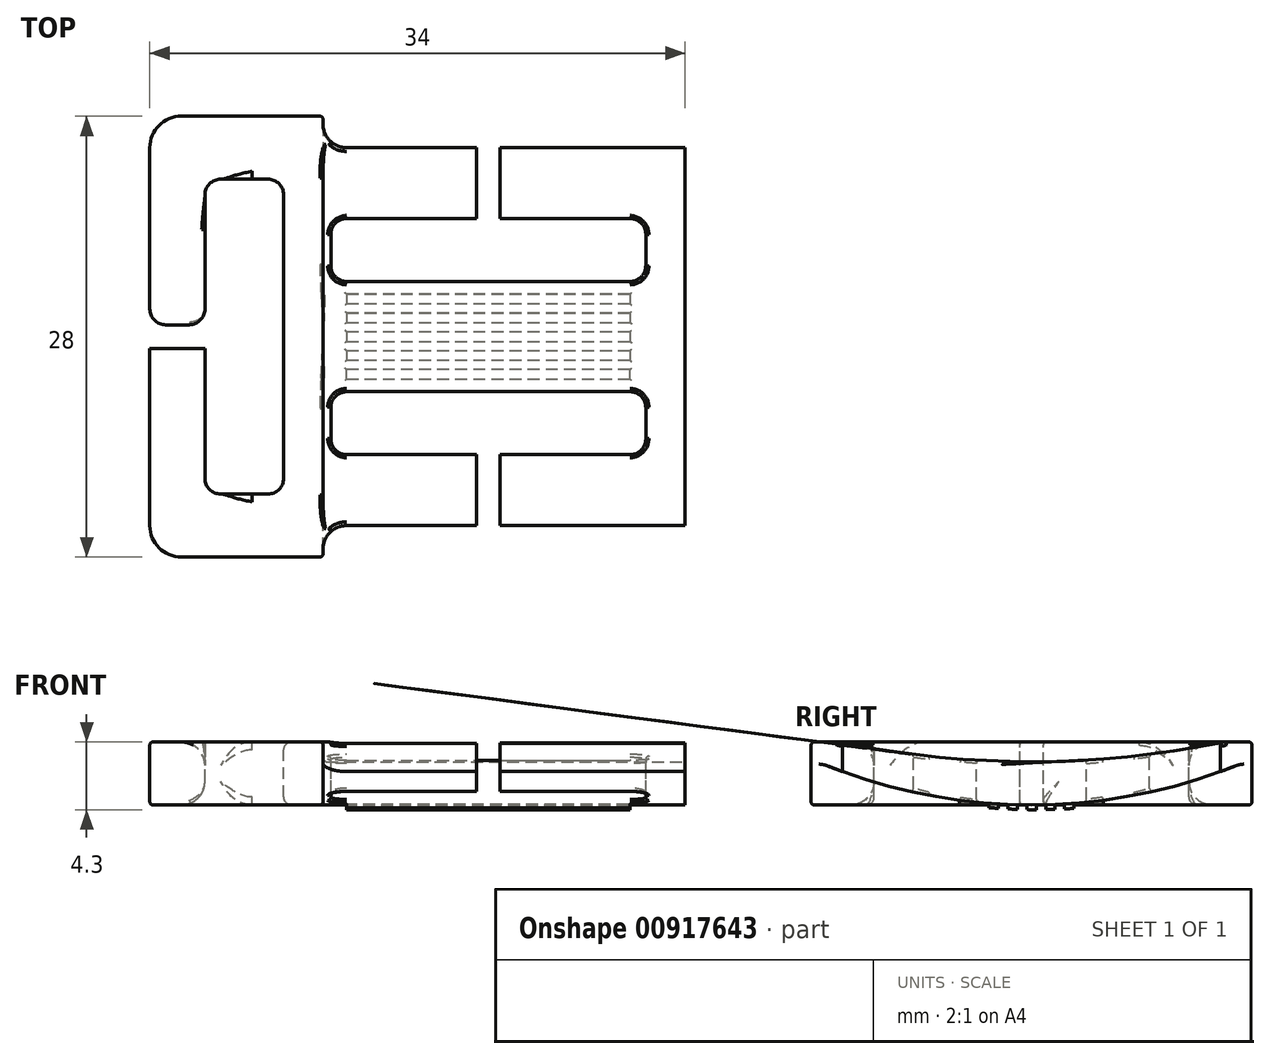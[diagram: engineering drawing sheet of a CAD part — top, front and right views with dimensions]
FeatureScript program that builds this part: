
annotation { "Feature Type Name" : "Feature", "Feature Type Description" : "" }
export const myFeature = defineFeature(function(context is Context, id is Id, definition is map)
    precondition{}
    {
        {
            var Q0;
            Q0=qCreatedBy(makeId("Top.planeOp"),FACE);
            var sketch = newSketch(context, id + "F0", { "sketchPlane" : qUnion([Q0])});
            skLineSegment(sketch, "E0.bottom", {"start": v(0, 0) * mm, "end": v(34, 0) * mm});
            skLineSegment(sketch, "E0.top", {"start": v(0, 28) * mm, "end": v(34, 28) * mm});
            skLineSegment(sketch, "E0.left", {"start": v(0, 0) * mm, "end": v(0, 28) * mm});
            skLineSegment(sketch, "E0.right", {"start": v(34, 0) * mm, "end": v(34, 28) * mm});
            skSolve(sketch);
        }
        {
            var Q0;
            Q0 = qSketchRegion(id + "F0", true);
            extrude(context, id + "F1", {"entities" : qUnion([Q0]), "depth" : 4 * mm, "offsetDistance" : 25 * mm});
        }
        {
            var Q0;
            Q0=makeQuery(id+"F1.opExtrude","CAP_FACE",FACE,{"disambiguationData":[OSD([sQuery(id+"F0.wireOp",EDGE,"E0.bottom"),sQuery(id+"F0.wireOp",EDGE,"E0.top"),sQuery(id+"F0.wireOp",EDGE,"E0.left"),sQuery(id+"F0.wireOp",EDGE,"E0.right")])],"isStart":false});
            var sketch = newSketch(context, id + "F2", { "sketchPlane" : qUnion([Q0])});
            skLineSegment(sketch, "E1.bottom", {"start": v(3.5, 24) * mm, "end": v(8.5, 24) * mm});
            skLineSegment(sketch, "E1.top", {"start": v(3.5, 4) * mm, "end": v(8.5, 4) * mm});
            skLineSegment(sketch, "E1.left", {"start": v(3.5, 24) * mm, "end": v(3.5, 4) * mm});
            skLineSegment(sketch, "E1.right", {"start": v(8.5, 24) * mm, "end": v(8.5, 4) * mm});
            skSolve(sketch);
        }
        {
            var Q0;
            Q0 = qSketchRegion(id + "F2", true);
            extrude(context, id + "F3", {"entities" : qUnion([Q0]), "operationType" : NewBodyOperationType.REMOVE, "endBound" : BoundingType.THROUGH_ALL, "oppositeDirection" : true, "depth" : 25 * mm, "offsetDistance" : 25 * mm});
        }
        {
            var Q0;
            Q0=makeQuery(id+"F1.opExtrude","CAP_FACE",FACE,{"disambiguationData":[OSD([sQuery(id+"F0.wireOp",EDGE,"E0.bottom"),sQuery(id+"F0.wireOp",EDGE,"E0.top"),sQuery(id+"F0.wireOp",EDGE,"E0.left"),sQuery(id+"F0.wireOp",EDGE,"E0.right")])],"isStart":false});
            var sketch = newSketch(context, id + "F4", { "sketchPlane" : qUnion([Q0])});
            skLineSegment(sketch, "E2.bottom", {"start": v(11.5, 21.5) * mm, "end": v(31.5, 21.5) * mm});
            skLineSegment(sketch, "E2.top", {"start": v(11.5, 17.5) * mm, "end": v(31.5, 17.5) * mm});
            skLineSegment(sketch, "E2.left", {"start": v(11.5, 21.5) * mm, "end": v(11.5, 17.5) * mm});
            skLineSegment(sketch, "E2.right", {"start": v(31.5, 21.5) * mm, "end": v(31.5, 17.5) * mm});
            skLineSegment(sketch, "E3.bottom", {"start": v(11.5, 10.5) * mm, "end": v(31.5, 10.5) * mm});
            skLineSegment(sketch, "E3.top", {"start": v(11.5, 6.5) * mm, "end": v(31.5, 6.5) * mm});
            skLineSegment(sketch, "E3.left", {"start": v(11.5, 10.5) * mm, "end": v(11.5, 6.5) * mm});
            skLineSegment(sketch, "E3.right", {"start": v(31.5, 10.5) * mm, "end": v(31.5, 6.5) * mm});
            skSolve(sketch);
        }
        {
            var Q0;
            Q0 = qSketchRegion(id + "F4", true);
            extrude(context, id + "F5", {"entities" : qUnion([Q0]), "operationType" : NewBodyOperationType.REMOVE, "endBound" : BoundingType.THROUGH_ALL, "oppositeDirection" : true, "depth" : 25 * mm, "offsetDistance" : 25 * mm});
        }
        {
            var Q0;
            Q0=makeQuery(id+"F1.opExtrude","CAP_FACE",FACE,{"disambiguationData":[OSD([sQuery(id+"F0.wireOp",EDGE,"E0.bottom"),sQuery(id+"F0.wireOp",EDGE,"E0.top"),sQuery(id+"F0.wireOp",EDGE,"E0.left"),sQuery(id+"F0.wireOp",EDGE,"E0.right")])],"isStart":false});
            var sketch = newSketch(context, id + "F6", { "sketchPlane" : qUnion([Q0])});
            skLineSegment(sketch, "E4.bottom", {"start": v(0, 13.25) * mm, "end": v(3.5, 13.25) * mm});
            skLineSegment(sketch, "E4.top", {"start": v(0, 14.75) * mm, "end": v(3.5, 14.75) * mm});
            skLineSegment(sketch, "E4.left", {"start": v(0, 13.25) * mm, "end": v(0, 14.75) * mm});
            skLineSegment(sketch, "E4.right", {"start": v(3.5, 13.25) * mm, "end": v(3.5, 14.75) * mm});
            skLineSegment(sketch, "E5.bottom", {"start": v(20.75, 28) * mm, "end": v(22.25, 28) * mm});
            skLineSegment(sketch, "E5.top", {"start": v(20.75, 21.5) * mm, "end": v(22.25, 21.5) * mm});
            skLineSegment(sketch, "E5.left", {"start": v(20.75, 28) * mm, "end": v(20.75, 21.5) * mm});
            skLineSegment(sketch, "E5.right", {"start": v(22.25, 28) * mm, "end": v(22.25, 21.5) * mm});
            skLineSegment(sketch, "E6.bottom", {"start": v(20.75, 6.5) * mm, "end": v(22.25, 6.5) * mm});
            skLineSegment(sketch, "E6.top", {"start": v(20.75, 0) * mm, "end": v(22.25, 0) * mm});
            skLineSegment(sketch, "E6.left", {"start": v(20.75, 6.5) * mm, "end": v(20.75, 0) * mm});
            skLineSegment(sketch, "E6.right", {"start": v(22.25, 6.5) * mm, "end": v(22.25, 0) * mm});
            skSolve(sketch);
        }
        {
            var Q0;
            Q0 = qSketchRegion(id + "F6", true);
            extrude(context, id + "F7", {"entities" : qUnion([Q0]), "operationType" : NewBodyOperationType.REMOVE, "endBound" : BoundingType.THROUGH_ALL, "oppositeDirection" : true, "depth" : 25 * mm, "offsetDistance" : 25 * mm});
        }
        {
            var Q0;
            Q0=makeQuery(id+"F5.boolean.opBoolean","COPY",EDGE,{"derivedFrom":makeQuery(id+"F5.opExtrude","SWEPT_EDGE",EDGE,{"disambiguationData":[OSD([sQuery(id+"F4.wireOp",EDGE,"E2.bottom"),sQuery(id+"F4.wireOp",EDGE,"E2.right")])]})});
            var Q1;
            Q1=makeQuery(id+"F5.boolean.opBoolean","COPY",EDGE,{"derivedFrom":makeQuery(id+"F5.opExtrude","SWEPT_EDGE",EDGE,{"disambiguationData":[OSD([sQuery(id+"F4.wireOp",EDGE,"E2.bottom"),sQuery(id+"F4.wireOp",EDGE,"E2.left")])]})});
            var Q2;
            Q2=makeQuery(id+"F5.boolean.opBoolean","COPY",EDGE,{"derivedFrom":makeQuery(id+"F5.opExtrude","SWEPT_EDGE",EDGE,{"disambiguationData":[OSD([sQuery(id+"F4.wireOp",EDGE,"E2.top"),sQuery(id+"F4.wireOp",EDGE,"E2.left")])]})});
            var Q3;
            Q3=makeQuery(id+"F5.boolean.opBoolean","COPY",EDGE,{"derivedFrom":makeQuery(id+"F5.opExtrude","SWEPT_EDGE",EDGE,{"disambiguationData":[OSD([sQuery(id+"F4.wireOp",EDGE,"E2.top"),sQuery(id+"F4.wireOp",EDGE,"E2.right")])]})});
            var Q4;
            Q4=makeQuery(id+"F5.boolean.opBoolean","COPY",EDGE,{"derivedFrom":makeQuery(id+"F5.opExtrude","SWEPT_EDGE",EDGE,{"disambiguationData":[OSD([sQuery(id+"F4.wireOp",EDGE,"E3.bottom"),sQuery(id+"F4.wireOp",EDGE,"E3.right")])]})});
            var Q5;
            Q5=makeQuery(id+"F5.boolean.opBoolean","COPY",EDGE,{"derivedFrom":makeQuery(id+"F5.opExtrude","SWEPT_EDGE",EDGE,{"disambiguationData":[OSD([sQuery(id+"F4.wireOp",EDGE,"E3.bottom"),sQuery(id+"F4.wireOp",EDGE,"E3.left")])]})});
            var Q6;
            Q6=makeQuery(id+"F5.boolean.opBoolean","COPY",EDGE,{"derivedFrom":makeQuery(id+"F5.opExtrude","SWEPT_EDGE",EDGE,{"disambiguationData":[OSD([sQuery(id+"F4.wireOp",EDGE,"E3.top"),sQuery(id+"F4.wireOp",EDGE,"E3.left")])]})});
            var Q7;
            Q7=makeQuery(id+"F5.boolean.opBoolean","COPY",EDGE,{"derivedFrom":makeQuery(id+"F5.opExtrude","SWEPT_EDGE",EDGE,{"disambiguationData":[OSD([sQuery(id+"F4.wireOp",EDGE,"E3.top"),sQuery(id+"F4.wireOp",EDGE,"E3.right")])]})});
            var Q8;
            Q8=makeQuery(id+"F3.boolean.opBoolean","COPY",EDGE,{"derivedFrom":makeQuery(id+"F3.opExtrude","SWEPT_EDGE",EDGE,{"disambiguationData":[OSD([sQuery(id+"F2.wireOp",EDGE,"E1.bottom"),sQuery(id+"F2.wireOp",EDGE,"E1.left")])]})});
            var Q9;
            Q9=makeQuery(id+"F3.boolean.opBoolean","COPY",EDGE,{"derivedFrom":makeQuery(id+"F3.opExtrude","SWEPT_EDGE",EDGE,{"disambiguationData":[OSD([sQuery(id+"F2.wireOp",EDGE,"E1.bottom"),sQuery(id+"F2.wireOp",EDGE,"E1.right")])]})});
            var Q10;
            Q10=makeQuery(id+"F3.boolean.opBoolean","COPY",EDGE,{"derivedFrom":makeQuery(id+"F3.opExtrude","SWEPT_EDGE",EDGE,{"disambiguationData":[OSD([sQuery(id+"F2.wireOp",EDGE,"E1.top"),sQuery(id+"F2.wireOp",EDGE,"E1.right")])]})});
            var Q11;
            Q11=makeQuery(id+"F3.boolean.opBoolean","COPY",EDGE,{"derivedFrom":makeQuery(id+"F3.opExtrude","SWEPT_EDGE",EDGE,{"disambiguationData":[OSD([sQuery(id+"F2.wireOp",EDGE,"E1.top"),sQuery(id+"F2.wireOp",EDGE,"E1.left")])]})});
            var Q12;
            Q12=makeQuery(id+"F7.boolean.opBoolean","COPY",EDGE,{"derivedFrom":makeQuery(id+"F7.opExtrude","SWEPT_EDGE",EDGE,{"disambiguationData":[OSD([sQuery(id+"F0.wireOp",EDGE,"E0.left"),sQuery(id+"F6.wireOp",EDGE,"E4.top"),sQuery(id+"F6.wireOp",EDGE,"E4.left")])]})});
            var Q13;
            Q13=makeQuery(id+"F7.boolean.opBoolean","COPY",EDGE,{"derivedFrom":makeQuery(id+"F7.opExtrude","SWEPT_EDGE",EDGE,{"disambiguationData":[OSD([sQuery(id+"F0.wireOp",EDGE,"E0.left"),sQuery(id+"F6.wireOp",EDGE,"E4.bottom"),sQuery(id+"F6.wireOp",EDGE,"E4.left")])]})});
            var Q14;
            Q14=makeQuery(id+"F7.boolean.opBoolean","COPY",EDGE,{"derivedFrom":makeQuery(id+"F7.opExtrude","SWEPT_EDGE",EDGE,{"disambiguationData":[OSD([sQuery(id+"F2.wireOp",EDGE,"E1.left"),sQuery(id+"F6.wireOp",EDGE,"E4.top"),sQuery(id+"F6.wireOp",EDGE,"E4.right")])]})});
            var Q15;
            Q15=makeQuery(id+"F7.boolean.opBoolean","COPY",EDGE,{"derivedFrom":makeQuery(id+"F7.opExtrude","SWEPT_EDGE",EDGE,{"disambiguationData":[OSD([sQuery(id+"F2.wireOp",EDGE,"E1.left"),sQuery(id+"F6.wireOp",EDGE,"E4.bottom"),sQuery(id+"F6.wireOp",EDGE,"E4.right")])]})});
            fillet(context, id + "F8", {"entities" : qUnion([Q0, Q1, Q2, Q3, Q4, Q5, Q6, Q7, Q8, Q9, Q10, Q11, Q12, Q13, Q14, Q15]), "radius" : 1 * mm, "tangentPropagation" : true, "allowEdgeOverflow" : false});
        }
        {
            var Q0;
            Q0=makeQuery(id+"F1.opExtrude","CAP_FACE",FACE,{"disambiguationData":[OSD([sQuery(id+"F0.wireOp",EDGE,"E0.bottom"),sQuery(id+"F0.wireOp",EDGE,"E0.top"),sQuery(id+"F0.wireOp",EDGE,"E0.left"),sQuery(id+"F0.wireOp",EDGE,"E0.right")])],"isStart":false});
            var sketch = newSketch(context, id + "F9", { "sketchPlane" : qUnion([Q0])});
            skLineSegment(sketch, "E7.bottom", {"start": v(11, 28) * mm, "end": v(34, 28) * mm});
            skLineSegment(sketch, "E7.top", {"start": v(11, 26) * mm, "end": v(34, 26) * mm});
            skLineSegment(sketch, "E7.left", {"start": v(11, 28) * mm, "end": v(11, 26) * mm});
            skLineSegment(sketch, "E7.right", {"start": v(34, 28) * mm, "end": v(34, 26) * mm});
            skLineSegment(sketch, "E8.bottom", {"start": v(11, 0) * mm, "end": v(34, 0) * mm});
            skLineSegment(sketch, "E8.top", {"start": v(11, 2) * mm, "end": v(34, 2) * mm});
            skLineSegment(sketch, "E8.left", {"start": v(11, 0) * mm, "end": v(11, 2) * mm});
            skLineSegment(sketch, "E8.right", {"start": v(34, 0) * mm, "end": v(34, 2) * mm});
            skSolve(sketch);
        }
        {
            var Q0;
            Q0 = qSketchRegion(id + "F9", true);
            extrude(context, id + "F10", {"entities" : qUnion([Q0]), "operationType" : NewBodyOperationType.REMOVE, "endBound" : BoundingType.THROUGH_ALL, "oppositeDirection" : true, "depth" : 25 * mm, "offsetDistance" : 25 * mm});
        }
        {
            var Q0;
            Q0=makeQuery(id+"F10.boolean.opBoolean","COPY",EDGE,{"derivedFrom":makeQuery(id+"F10.opExtrude","SWEPT_EDGE",EDGE,{"disambiguationData":[OSD([sQuery(id+"F9.wireOp",EDGE,"E7.top"),sQuery(id+"F9.wireOp",EDGE,"E7.left")])]})});
            var Q1;
            Q1=makeQuery(id+"F10.boolean.opBoolean","COPY",EDGE,{"derivedFrom":makeQuery(id+"F10.opExtrude","SWEPT_EDGE",EDGE,{"disambiguationData":[OSD([sQuery(id+"F9.wireOp",EDGE,"E8.top"),sQuery(id+"F9.wireOp",EDGE,"E8.left")])]})});
            var Q2;
            Q2=makeQuery(id+"F10.boolean.opBoolean","COPY",EDGE,{"derivedFrom":makeQuery(id+"F10.opExtrude","SWEPT_EDGE",EDGE,{"disambiguationData":[OSD([sQuery(id+"F0.wireOp",EDGE,"E0.right"),sQuery(id+"F9.wireOp",EDGE,"E8.top"),sQuery(id+"F9.wireOp",EDGE,"E8.right")])]})});
            var Q3;
            Q3=makeQuery(id+"F10.boolean.opBoolean","COPY",EDGE,{"derivedFrom":makeQuery(id+"F10.opExtrude","SWEPT_EDGE",EDGE,{"disambiguationData":[OSD([sQuery(id+"F0.wireOp",EDGE,"E0.right"),sQuery(id+"F9.wireOp",EDGE,"E7.top"),sQuery(id+"F9.wireOp",EDGE,"E7.right")])]})});
            fillet(context, id + "F11", {"entities" : qUnion([Q0, Q1, Q2, Q3]), "radius" : 1.5 * mm, "tangentPropagation" : true, "allowEdgeOverflow" : false});
        }
        {
            var Q0;
            Q0=makeQuery(id+"F10.boolean.opBoolean","COPY",EDGE,{"derivedFrom":makeQuery(id+"F10.opExtrude","SWEPT_EDGE",EDGE,{"disambiguationData":[OSD([sQuery(id+"F0.wireOp",EDGE,"E0.top"),sQuery(id+"F9.wireOp",EDGE,"E7.bottom"),sQuery(id+"F9.wireOp",EDGE,"E7.left")])]})});
            var Q1;
            Q1=makeQuery(id+"F1.opExtrude","SWEPT_EDGE",EDGE,{"disambiguationData":[OSD([sQuery(id+"F0.wireOp",EDGE,"E0.top"),sQuery(id+"F0.wireOp",EDGE,"E0.left")])]});
            var Q2;
            Q2=makeQuery(id+"F1.opExtrude","SWEPT_EDGE",EDGE,{"disambiguationData":[OSD([sQuery(id+"F0.wireOp",EDGE,"E0.bottom"),sQuery(id+"F0.wireOp",EDGE,"E0.left")])]});
            var Q3;
            Q3=makeQuery(id+"F10.boolean.opBoolean","COPY",EDGE,{"derivedFrom":makeQuery(id+"F10.opExtrude","SWEPT_EDGE",EDGE,{"disambiguationData":[OSD([sQuery(id+"F0.wireOp",EDGE,"E0.bottom"),sQuery(id+"F9.wireOp",EDGE,"E8.bottom"),sQuery(id+"F9.wireOp",EDGE,"E8.left")])]})});
            fillet(context, id + "F12", {"entities" : qUnion([Q0, Q1, Q2, Q3]), "radius" : 2 * mm, "tangentPropagation" : true, "allowEdgeOverflow" : false});
        }
        {
            var Q0;
            Q0=makeQuery(id+"F1.opExtrude","SWEPT_FACE",FACE,{"disambiguationData":[OSD([sQuery(id+"F0.wireOp",EDGE,"E0.right")])]});
            var sketch = newSketch(context, id + "F13", { "sketchPlane" : qUnion([Q0])});
            skCircle(sketch, "E9", {"center": v(14, 63) * mm, "radius": 60.25 * mm});
            skPoint(sketch, "E9.centerSnap0", {"position": v(14, 4) * mm});
            skSolve(sketch);
        }
        {
            var Q0;
            Q0 = qSketchRegion(id + "F13", true);
            extrude(context, id + "F14", {"entities" : qUnion([Q0]), "operationType" : NewBodyOperationType.REMOVE, "oppositeDirection" : true, "depth" : 23 * mm, "offsetDistance" : 25 * mm});
        }
        {
            var Q0;
            Q0=makeQuery(id+"F1.opExtrude","SWEPT_FACE",FACE,{"disambiguationData":[OSD([sQuery(id+"F0.wireOp",EDGE,"E0.right")])]});
            var sketch = newSketch(context, id + "F15", { "sketchPlane" : qUnion([Q0])});
            skCircle(sketch, "E10", {"center": v(14, 35) * mm, "radius": 35 * mm});
            skPoint(sketch, "E10.centerSnap0", {"position": v(14, 2.75) * mm});
            skCircle(sketch, "E11", {"center": v(14, 35) * mm, "radius": 50 * mm});
            skSolve(sketch);
        }
        {
            var Q0;
            Q0=makeQuery(id+"F15.imprint","IMPRINT",FACE,{"disambiguationData":[TD([[makeQuery(id+"F15.imprint","IMPRINT",EDGE,{"derivedFrom":sQuery(id+"F15.wireOp",EDGE,"E11")}),1.0]])]});
            var Q1;
            Q1=makeQuery(id+"F14.boolean.opBoolean","COPY",FACE,{"derivedFrom":makeQuery(id+"F14.opExtrude","CAP_FACE",FACE,{"disambiguationData":[OSD([sQuery(id+"F13.wireOp",EDGE,"E9")])],"isStart":false})});
            extrude(context, id + "F16", {"entities" : qUnion([Q0]), "operationType" : NewBodyOperationType.REMOVE, "endBound" : BoundingType.UP_TO_SURFACE, "oppositeDirection" : true, "depth" : 25 * mm, "endBoundEntityFace" : qUnion([Q1]), "offsetDistance" : 25 * mm});
        }
        {
            var Q0;
            {var subQ0=sQuery(id+"F15.wireOp",EDGE,"E10");var subQ1=sQuery(id+"F0.wireOp",EDGE,"E0.right");var subQ2=makeQuery(id+"F1.opExtrude","CAP_EDGE",EDGE,{"disambiguationData":[OSD([subQ1])],"isStart":true});var subQ3=makeQuery(id+"F15.imprint","INTERSECT",VERTEX,{"derivedFrom":[subQ2,subQ0]});Q0=makeQuery(id+"F15.imprint","IMPRINT",FACE,{"disambiguationData":[TD([[makeQuery(id+"F15.imprint","IMPRINT",EDGE,{"disambiguationData":[TD([[subQ3,1.0]])],"derivedFrom":subQ0}),-1.0]])]});}
            var Q1;
            {var subQ0=sQuery(id+"F15.wireOp",EDGE,"E10");var subQ1=sQuery(id+"F0.wireOp",EDGE,"E0.right");var subQ2=makeQuery(id+"F1.opExtrude","CAP_EDGE",EDGE,{"disambiguationData":[OSD([subQ1])],"isStart":true});var subQ3=makeQuery(id+"F15.imprint","INTERSECT",VERTEX,{"derivedFrom":[subQ2,subQ0]});Q1=makeQuery(id+"F15.imprint","IMPRINT",FACE,{"disambiguationData":[TD([[makeQuery(id+"F15.imprint","IMPRINT",EDGE,{"disambiguationData":[TD([[subQ3,-1.0]])],"derivedFrom":subQ0}),-1.0]])]});}
            var Q2;
            Q2=makeQuery(id+"F15.imprint","IMPRINT",FACE,{"disambiguationData":[TD([[makeQuery(id+"F15.imprint","IMPRINT",EDGE,{"derivedFrom":sQuery(id+"F15.wireOp",EDGE,"E11")}),1.0]])]});
            var Q3;
            Q3=makeQuery(id+"F14.boolean.opBoolean","COPY",FACE,{"derivedFrom":makeQuery(id+"F14.opExtrude","CAP_FACE",FACE,{"disambiguationData":[OSD([sQuery(id+"F13.wireOp",EDGE,"E9")])],"isStart":false})});
            extrude(context, id + "F17", {"entities" : qUnion([Q0, Q1, Q2]), "operationType" : NewBodyOperationType.REMOVE, "endBound" : BoundingType.UP_TO_SURFACE, "oppositeDirection" : true, "depth" : 25 * mm, "endBoundEntityFace" : qUnion([Q3]), "offsetDistance" : 25 * mm});
        }
        {
            var Q0;
            Q0=qCreatedBy(makeId("Top.planeOp"),FACE);
            var sketch = newSketch(context, id + "F18", { "sketchPlane" : qUnion([Q0])});
            skLineSegment(sketch, "E12.bottom", {"start": v(12.5, 13.7) * mm, "end": v(30.5, 13.7) * mm});
            skLineSegment(sketch, "E12.top", {"start": v(12.5, 14.3) * mm, "end": v(30.5, 14.3) * mm});
            skLineSegment(sketch, "E12.left", {"start": v(12.5, 13.7) * mm, "end": v(12.5, 14.3) * mm});
            skLineSegment(sketch, "E12.right", {"start": v(30.5, 13.7) * mm, "end": v(30.5, 14.3) * mm});
            skLineSegment(sketch, "E13.bottom", {"start": v(12.5, 14.9) * mm, "end": v(30.5, 14.9) * mm});
            skLineSegment(sketch, "E13.top", {"start": v(12.5, 15.5) * mm, "end": v(30.5, 15.5) * mm});
            skLineSegment(sketch, "E13.left", {"start": v(12.5, 14.9) * mm, "end": v(12.5, 15.5) * mm});
            skLineSegment(sketch, "E13.right", {"start": v(30.5, 14.9) * mm, "end": v(30.5, 15.5) * mm});
            skLineSegment(sketch, "E14.bottom", {"start": v(12.5, 16.1) * mm, "end": v(30.5, 16.1) * mm});
            skLineSegment(sketch, "E14.top", {"start": v(12.5, 16.7) * mm, "end": v(30.5, 16.7) * mm});
            skLineSegment(sketch, "E14.left", {"start": v(12.5, 16.1) * mm, "end": v(12.5, 16.7) * mm});
            skLineSegment(sketch, "E14.right", {"start": v(30.5, 16.1) * mm, "end": v(30.5, 16.7) * mm});
            skLineSegment(sketch, "E15.bottom", {"start": v(12.5, 12.5) * mm, "end": v(30.5, 12.5) * mm});
            skLineSegment(sketch, "E15.top", {"start": v(12.5, 13.1) * mm, "end": v(30.5, 13.1) * mm});
            skLineSegment(sketch, "E15.left", {"start": v(12.5, 12.5) * mm, "end": v(12.5, 13.1) * mm});
            skLineSegment(sketch, "E15.right", {"start": v(30.5, 12.5) * mm, "end": v(30.5, 13.1) * mm});
            skLineSegment(sketch, "E16.bottom", {"start": v(12.5, 11.9) * mm, "end": v(30.5, 11.9) * mm});
            skLineSegment(sketch, "E16.top", {"start": v(12.5, 11.3) * mm, "end": v(30.5, 11.3) * mm});
            skLineSegment(sketch, "E16.left", {"start": v(12.5, 11.9) * mm, "end": v(12.5, 11.3) * mm});
            skLineSegment(sketch, "E16.right", {"start": v(30.5, 11.9) * mm, "end": v(30.5, 11.3) * mm});
            skSolve(sketch);
        }
        {
            var Q0;
            Q0 = qSketchRegion(id + "F18", true);
            extrude(context, id + "F19", {"entities" : qUnion([Q0]), "operationType" : NewBodyOperationType.ADD, "depth" : 0.2 * mm, "offsetDistance" : 25 * mm, "hasSecondDirection" : true, "secondDirectionOppositeDirection" : true, "secondDirectionDepth" : 2 * mm});
        }
        {
            var Q0;
            Q0=makeQuery(id+"F1.opExtrude","SWEPT_FACE",FACE,{"disambiguationData":[OSD([sQuery(id+"F0.wireOp",EDGE,"E0.right")])]});
            var sketch = newSketch(context, id + "F20", { "sketchPlane" : qUnion([Q0])});
            skCircle(sketch, "E17", {"center": v(14.3, 35) * mm, "radius": 35.3 * mm});
            skPoint(sketch, "E17.centerSnap0", {"position": v(14.3, 0) * mm});
            skCircle(sketch, "E18", {"center": v(14.3, 35) * mm, "radius": 50 * mm});
            skSolve(sketch);
        }
        {
            var Q0;
            Q0=makeQuery(id+"F20.imprint","IMPRINT",FACE,{"disambiguationData":[TD([[makeQuery(id+"F20.imprint","IMPRINT",EDGE,{"derivedFrom":sQuery(id+"F20.wireOp",EDGE,"E17")}),-1.0]])]});
            var Q1;
            {var subQ0=sQuery(id+"F15.wireOp",EDGE,"E11");var subQ1=sQuery(id+"F15.wireOp",EDGE,"E10");var subQ2=sQuery(id+"F0.wireOp",EDGE,"E0.right");var subQ3=sQuery(id+"F0.wireOp",EDGE,"E0.bottom");var subQ4=sQuery(id+"F9.wireOp",EDGE,"E8.right");var subQ5=sQuery(id+"F9.wireOp",EDGE,"E8.top");Q1=makeQuery(id+"F17.boolean.opBoolean","MERGE",FACE,{"derivedFrom":[makeQuery(id+"F16.boolean.opBoolean","COPY",FACE,{"disambiguationData":[TD([makeQuery(id+"F12.opFillet","BLEND_FACE",FACE,{"disambiguationData":[OSD([subQ3,sQuery(id+"F9.wireOp",EDGE,"E8.bottom"),sQuery(id+"F9.wireOp",EDGE,"E8.left")])]})])],"derivedFrom":makeQuery(id+"F16.opExtrude","CAP_FACE",FACE,{"disambiguationData":[OSD([subQ2,sQuery(id+"F9.wireOp",EDGE,"E7.top"),sQuery(id+"F9.wireOp",EDGE,"E7.right"),subQ5,subQ4,subQ1,subQ0])],"isStart":false})})],"fromTools":[makeQuery(id+"F17.opExtrude","CAP_FACE",FACE,{"disambiguationData":[OSD([subQ1,subQ0])],"isStart":false})]});}
            extrude(context, id + "F21", {"entities" : qUnion([Q0]), "operationType" : NewBodyOperationType.REMOVE, "endBound" : BoundingType.UP_TO_SURFACE, "oppositeDirection" : true, "depth" : 25 * mm, "endBoundEntityFace" : qUnion([Q1]), "offsetDistance" : 25 * mm});
        }
        {
            var Q0;
            {var subQ0=sQuery(id+"F15.wireOp",EDGE,"E10");Q0=makeQuery(id+"F17.boolean.opBoolean","MERGE",EDGE,{"derivedFrom":[makeQuery(id+"F16.boolean.opBoolean","COPY",EDGE,{"disambiguationData":[TD([makeQuery(id+"F12.opFillet","BLEND_FACE",FACE,{"disambiguationData":[OSD([sQuery(id+"F0.wireOp",EDGE,"E0.top"),sQuery(id+"F9.wireOp",EDGE,"E7.bottom"),sQuery(id+"F9.wireOp",EDGE,"E7.left")])]})])],"derivedFrom":makeQuery(id+"F16.opExtrude","CAP_EDGE",EDGE,{"disambiguationData":[OSD([subQ0])],"isStart":false})})],"fromTools":[makeQuery(id+"F17.opExtrude","CAP_EDGE",EDGE,{"disambiguationData":[OSD([subQ0])],"isStart":false})]});}
            var Q1;
            {var subQ0=sQuery(id+"F15.wireOp",EDGE,"E10");Q1=makeQuery(id+"F17.boolean.opBoolean","MERGE",EDGE,{"derivedFrom":[makeQuery(id+"F16.boolean.opBoolean","COPY",EDGE,{"disambiguationData":[TD([makeQuery(id+"F12.opFillet","BLEND_FACE",FACE,{"disambiguationData":[OSD([sQuery(id+"F0.wireOp",EDGE,"E0.bottom"),sQuery(id+"F9.wireOp",EDGE,"E8.bottom"),sQuery(id+"F9.wireOp",EDGE,"E8.left")])]})])],"derivedFrom":makeQuery(id+"F16.opExtrude","CAP_EDGE",EDGE,{"disambiguationData":[OSD([subQ0])],"isStart":false})})],"fromTools":[makeQuery(id+"F17.opExtrude","CAP_EDGE",EDGE,{"disambiguationData":[OSD([subQ0])],"isStart":false})]});}
            var Q2;
            {var subQ0=sQuery(id+"F15.wireOp",EDGE,"E10");var subQ4=makeQuery(id+"F7.boolean.opBoolean","COPY",FACE,{"derivedFrom":makeQuery(id+"F7.opExtrude","SWEPT_FACE",FACE,{"disambiguationData":[OSD([sQuery(id+"F6.wireOp",EDGE,"E6.left")])]})});var subQ16=makeQuery(id+"F16.opExtrude","SWEPT_FACE",FACE,{"disambiguationData":[OSD([subQ0])]});var subQ18=makeQuery(id+"F7.boolean.opBoolean","COPY",FACE,{"derivedFrom":makeQuery(id+"F7.opExtrude","SWEPT_FACE",FACE,{"disambiguationData":[OSD([sQuery(id+"F6.wireOp",EDGE,"E5.left")])]})});var subQ21=makeQuery(id+"F7.boolean.opBoolean","COPY",FACE,{"derivedFrom":makeQuery(id+"F7.opExtrude","SWEPT_FACE",FACE,{"disambiguationData":[OSD([sQuery(id+"F6.wireOp",EDGE,"E6.right")])]})});var subQ23=makeQuery(id+"F7.boolean.opBoolean","COPY",FACE,{"derivedFrom":makeQuery(id+"F7.opExtrude","SWEPT_FACE",FACE,{"disambiguationData":[OSD([sQuery(id+"F6.wireOp",EDGE,"E5.right")])]})});Q2=makeQuery(id+"F19.boolean.opBoolean","INTERSECT",EDGE,{"derivedFrom":[makeQuery(id+"F17.boolean.opBoolean","MERGE",FACE,{"derivedFrom":[makeQuery(id+"F16.boolean.opBoolean","COPY",FACE,{"disambiguationData":[TD([subQ23])],"derivedFrom":subQ16}),makeQuery(id+"F16.boolean.opBoolean","COPY",FACE,{"disambiguationData":[TD([subQ21])],"derivedFrom":subQ16}),makeQuery(id+"F16.boolean.opBoolean","COPY",FACE,{"disambiguationData":[TD([subQ18])],"derivedFrom":subQ16}),makeQuery(id+"F16.boolean.opBoolean","COPY",FACE,{"disambiguationData":[TD([subQ4])],"derivedFrom":subQ16})],"fromTools":[makeQuery(id+"F17.opExtrude","SWEPT_FACE",FACE,{"disambiguationData":[OSD([subQ0])]})]}),makeQuery(id+"F19.opExtrude","SWEPT_FACE",FACE,{"disambiguationData":[OSD([sQuery(id+"F18.wireOp",EDGE,"GZ6DawBn-dVhs-ftJf-icQb-t5xCzbtVKISh.top")])]})]});}
            var Q3;
            {var subQ0=sQuery(id+"F15.wireOp",EDGE,"E10");var subQ4=makeQuery(id+"F7.boolean.opBoolean","COPY",FACE,{"derivedFrom":makeQuery(id+"F7.opExtrude","SWEPT_FACE",FACE,{"disambiguationData":[OSD([sQuery(id+"F6.wireOp",EDGE,"E6.left")])]})});var subQ16=makeQuery(id+"F16.opExtrude","SWEPT_FACE",FACE,{"disambiguationData":[OSD([subQ0])]});var subQ18=makeQuery(id+"F7.boolean.opBoolean","COPY",FACE,{"derivedFrom":makeQuery(id+"F7.opExtrude","SWEPT_FACE",FACE,{"disambiguationData":[OSD([sQuery(id+"F6.wireOp",EDGE,"E5.left")])]})});var subQ21=makeQuery(id+"F7.boolean.opBoolean","COPY",FACE,{"derivedFrom":makeQuery(id+"F7.opExtrude","SWEPT_FACE",FACE,{"disambiguationData":[OSD([sQuery(id+"F6.wireOp",EDGE,"E6.right")])]})});var subQ23=makeQuery(id+"F7.boolean.opBoolean","COPY",FACE,{"derivedFrom":makeQuery(id+"F7.opExtrude","SWEPT_FACE",FACE,{"disambiguationData":[OSD([sQuery(id+"F6.wireOp",EDGE,"E5.right")])]})});Q3=makeQuery(id+"F19.boolean.opBoolean","INTERSECT",EDGE,{"derivedFrom":[makeQuery(id+"F17.boolean.opBoolean","MERGE",FACE,{"derivedFrom":[makeQuery(id+"F16.boolean.opBoolean","COPY",FACE,{"disambiguationData":[TD([subQ23])],"derivedFrom":subQ16}),makeQuery(id+"F16.boolean.opBoolean","COPY",FACE,{"disambiguationData":[TD([subQ21])],"derivedFrom":subQ16}),makeQuery(id+"F16.boolean.opBoolean","COPY",FACE,{"disambiguationData":[TD([subQ18])],"derivedFrom":subQ16}),makeQuery(id+"F16.boolean.opBoolean","COPY",FACE,{"disambiguationData":[TD([subQ4])],"derivedFrom":subQ16})],"fromTools":[makeQuery(id+"F17.opExtrude","SWEPT_FACE",FACE,{"disambiguationData":[OSD([subQ0])]})]}),makeQuery(id+"F19.opExtrude","SWEPT_FACE",FACE,{"disambiguationData":[OSD([sQuery(id+"F18.wireOp",EDGE,"bdn7c9yY-9ESb-mA8W-PJno-jlEChpIoJOdE.top")])]})]});}
            var Q4;
            {var subQ0=sQuery(id+"F15.wireOp",EDGE,"E10");var subQ4=makeQuery(id+"F7.boolean.opBoolean","COPY",FACE,{"derivedFrom":makeQuery(id+"F7.opExtrude","SWEPT_FACE",FACE,{"disambiguationData":[OSD([sQuery(id+"F6.wireOp",EDGE,"E6.left")])]})});var subQ16=makeQuery(id+"F16.opExtrude","SWEPT_FACE",FACE,{"disambiguationData":[OSD([subQ0])]});var subQ18=makeQuery(id+"F7.boolean.opBoolean","COPY",FACE,{"derivedFrom":makeQuery(id+"F7.opExtrude","SWEPT_FACE",FACE,{"disambiguationData":[OSD([sQuery(id+"F6.wireOp",EDGE,"E5.left")])]})});var subQ21=makeQuery(id+"F7.boolean.opBoolean","COPY",FACE,{"derivedFrom":makeQuery(id+"F7.opExtrude","SWEPT_FACE",FACE,{"disambiguationData":[OSD([sQuery(id+"F6.wireOp",EDGE,"E6.right")])]})});var subQ23=makeQuery(id+"F7.boolean.opBoolean","COPY",FACE,{"derivedFrom":makeQuery(id+"F7.opExtrude","SWEPT_FACE",FACE,{"disambiguationData":[OSD([sQuery(id+"F6.wireOp",EDGE,"E5.right")])]})});Q4=makeQuery(id+"F19.boolean.opBoolean","INTERSECT",EDGE,{"derivedFrom":[makeQuery(id+"F17.boolean.opBoolean","MERGE",FACE,{"derivedFrom":[makeQuery(id+"F16.boolean.opBoolean","COPY",FACE,{"disambiguationData":[TD([subQ23])],"derivedFrom":subQ16}),makeQuery(id+"F16.boolean.opBoolean","COPY",FACE,{"disambiguationData":[TD([subQ21])],"derivedFrom":subQ16}),makeQuery(id+"F16.boolean.opBoolean","COPY",FACE,{"disambiguationData":[TD([subQ18])],"derivedFrom":subQ16}),makeQuery(id+"F16.boolean.opBoolean","COPY",FACE,{"disambiguationData":[TD([subQ4])],"derivedFrom":subQ16})],"fromTools":[makeQuery(id+"F17.opExtrude","SWEPT_FACE",FACE,{"disambiguationData":[OSD([subQ0])]})]}),makeQuery(id+"F19.opExtrude","SWEPT_FACE",FACE,{"disambiguationData":[OSD([sQuery(id+"F18.wireOp",EDGE,"3WnHr87n-zB70-hSeO-Aol3-sTKqONvJ2aJL.top")])]})]});}
            var Q5;
            {var subQ0=sQuery(id+"F15.wireOp",EDGE,"E10");var subQ4=makeQuery(id+"F7.boolean.opBoolean","COPY",FACE,{"derivedFrom":makeQuery(id+"F7.opExtrude","SWEPT_FACE",FACE,{"disambiguationData":[OSD([sQuery(id+"F6.wireOp",EDGE,"E6.left")])]})});var subQ16=makeQuery(id+"F16.opExtrude","SWEPT_FACE",FACE,{"disambiguationData":[OSD([subQ0])]});var subQ18=makeQuery(id+"F7.boolean.opBoolean","COPY",FACE,{"derivedFrom":makeQuery(id+"F7.opExtrude","SWEPT_FACE",FACE,{"disambiguationData":[OSD([sQuery(id+"F6.wireOp",EDGE,"E5.left")])]})});var subQ21=makeQuery(id+"F7.boolean.opBoolean","COPY",FACE,{"derivedFrom":makeQuery(id+"F7.opExtrude","SWEPT_FACE",FACE,{"disambiguationData":[OSD([sQuery(id+"F6.wireOp",EDGE,"E6.right")])]})});var subQ23=makeQuery(id+"F7.boolean.opBoolean","COPY",FACE,{"derivedFrom":makeQuery(id+"F7.opExtrude","SWEPT_FACE",FACE,{"disambiguationData":[OSD([sQuery(id+"F6.wireOp",EDGE,"E5.right")])]})});Q5=makeQuery(id+"F19.boolean.opBoolean","INTERSECT",EDGE,{"derivedFrom":[makeQuery(id+"F17.boolean.opBoolean","MERGE",FACE,{"derivedFrom":[makeQuery(id+"F16.boolean.opBoolean","COPY",FACE,{"disambiguationData":[TD([subQ23])],"derivedFrom":subQ16}),makeQuery(id+"F16.boolean.opBoolean","COPY",FACE,{"disambiguationData":[TD([subQ21])],"derivedFrom":subQ16}),makeQuery(id+"F16.boolean.opBoolean","COPY",FACE,{"disambiguationData":[TD([subQ18])],"derivedFrom":subQ16}),makeQuery(id+"F16.boolean.opBoolean","COPY",FACE,{"disambiguationData":[TD([subQ4])],"derivedFrom":subQ16})],"fromTools":[makeQuery(id+"F17.opExtrude","SWEPT_FACE",FACE,{"disambiguationData":[OSD([subQ0])]})]}),makeQuery(id+"F19.opExtrude","SWEPT_FACE",FACE,{"disambiguationData":[OSD([sQuery(id+"F18.wireOp",EDGE,"E14.top")])]})]});}
            var Q6;
            {var subQ0=sQuery(id+"F15.wireOp",EDGE,"E10");var subQ4=makeQuery(id+"F7.boolean.opBoolean","COPY",FACE,{"derivedFrom":makeQuery(id+"F7.opExtrude","SWEPT_FACE",FACE,{"disambiguationData":[OSD([sQuery(id+"F6.wireOp",EDGE,"E6.left")])]})});var subQ16=makeQuery(id+"F16.opExtrude","SWEPT_FACE",FACE,{"disambiguationData":[OSD([subQ0])]});var subQ18=makeQuery(id+"F7.boolean.opBoolean","COPY",FACE,{"derivedFrom":makeQuery(id+"F7.opExtrude","SWEPT_FACE",FACE,{"disambiguationData":[OSD([sQuery(id+"F6.wireOp",EDGE,"E5.left")])]})});var subQ21=makeQuery(id+"F7.boolean.opBoolean","COPY",FACE,{"derivedFrom":makeQuery(id+"F7.opExtrude","SWEPT_FACE",FACE,{"disambiguationData":[OSD([sQuery(id+"F6.wireOp",EDGE,"E6.right")])]})});var subQ23=makeQuery(id+"F7.boolean.opBoolean","COPY",FACE,{"derivedFrom":makeQuery(id+"F7.opExtrude","SWEPT_FACE",FACE,{"disambiguationData":[OSD([sQuery(id+"F6.wireOp",EDGE,"E5.right")])]})});Q6=makeQuery(id+"F19.boolean.opBoolean","INTERSECT",EDGE,{"derivedFrom":[makeQuery(id+"F17.boolean.opBoolean","MERGE",FACE,{"derivedFrom":[makeQuery(id+"F16.boolean.opBoolean","COPY",FACE,{"disambiguationData":[TD([subQ23])],"derivedFrom":subQ16}),makeQuery(id+"F16.boolean.opBoolean","COPY",FACE,{"disambiguationData":[TD([subQ21])],"derivedFrom":subQ16}),makeQuery(id+"F16.boolean.opBoolean","COPY",FACE,{"disambiguationData":[TD([subQ18])],"derivedFrom":subQ16}),makeQuery(id+"F16.boolean.opBoolean","COPY",FACE,{"disambiguationData":[TD([subQ4])],"derivedFrom":subQ16})],"fromTools":[makeQuery(id+"F17.opExtrude","SWEPT_FACE",FACE,{"disambiguationData":[OSD([subQ0])]})]}),makeQuery(id+"F19.opExtrude","SWEPT_FACE",FACE,{"disambiguationData":[OSD([sQuery(id+"F18.wireOp",EDGE,"E13.top")])]})]});}
            var Q7;
            {var subQ0=sQuery(id+"F15.wireOp",EDGE,"E10");var subQ4=makeQuery(id+"F7.boolean.opBoolean","COPY",FACE,{"derivedFrom":makeQuery(id+"F7.opExtrude","SWEPT_FACE",FACE,{"disambiguationData":[OSD([sQuery(id+"F6.wireOp",EDGE,"E6.left")])]})});var subQ16=makeQuery(id+"F16.opExtrude","SWEPT_FACE",FACE,{"disambiguationData":[OSD([subQ0])]});var subQ18=makeQuery(id+"F7.boolean.opBoolean","COPY",FACE,{"derivedFrom":makeQuery(id+"F7.opExtrude","SWEPT_FACE",FACE,{"disambiguationData":[OSD([sQuery(id+"F6.wireOp",EDGE,"E5.left")])]})});var subQ21=makeQuery(id+"F7.boolean.opBoolean","COPY",FACE,{"derivedFrom":makeQuery(id+"F7.opExtrude","SWEPT_FACE",FACE,{"disambiguationData":[OSD([sQuery(id+"F6.wireOp",EDGE,"E6.right")])]})});var subQ23=makeQuery(id+"F7.boolean.opBoolean","COPY",FACE,{"derivedFrom":makeQuery(id+"F7.opExtrude","SWEPT_FACE",FACE,{"disambiguationData":[OSD([sQuery(id+"F6.wireOp",EDGE,"E5.right")])]})});Q7=makeQuery(id+"F19.boolean.opBoolean","INTERSECT",EDGE,{"derivedFrom":[makeQuery(id+"F17.boolean.opBoolean","MERGE",FACE,{"derivedFrom":[makeQuery(id+"F16.boolean.opBoolean","COPY",FACE,{"disambiguationData":[TD([subQ23])],"derivedFrom":subQ16}),makeQuery(id+"F16.boolean.opBoolean","COPY",FACE,{"disambiguationData":[TD([subQ21])],"derivedFrom":subQ16}),makeQuery(id+"F16.boolean.opBoolean","COPY",FACE,{"disambiguationData":[TD([subQ18])],"derivedFrom":subQ16}),makeQuery(id+"F16.boolean.opBoolean","COPY",FACE,{"disambiguationData":[TD([subQ4])],"derivedFrom":subQ16})],"fromTools":[makeQuery(id+"F17.opExtrude","SWEPT_FACE",FACE,{"disambiguationData":[OSD([subQ0])]})]}),makeQuery(id+"F19.opExtrude","SWEPT_FACE",FACE,{"disambiguationData":[OSD([sQuery(id+"F18.wireOp",EDGE,"E12.top")])]})]});}
            var Q8;
            {var subQ0=sQuery(id+"F15.wireOp",EDGE,"E10");var subQ4=makeQuery(id+"F7.boolean.opBoolean","COPY",FACE,{"derivedFrom":makeQuery(id+"F7.opExtrude","SWEPT_FACE",FACE,{"disambiguationData":[OSD([sQuery(id+"F6.wireOp",EDGE,"E6.left")])]})});var subQ16=makeQuery(id+"F16.opExtrude","SWEPT_FACE",FACE,{"disambiguationData":[OSD([subQ0])]});var subQ18=makeQuery(id+"F7.boolean.opBoolean","COPY",FACE,{"derivedFrom":makeQuery(id+"F7.opExtrude","SWEPT_FACE",FACE,{"disambiguationData":[OSD([sQuery(id+"F6.wireOp",EDGE,"E5.left")])]})});var subQ21=makeQuery(id+"F7.boolean.opBoolean","COPY",FACE,{"derivedFrom":makeQuery(id+"F7.opExtrude","SWEPT_FACE",FACE,{"disambiguationData":[OSD([sQuery(id+"F6.wireOp",EDGE,"E6.right")])]})});var subQ23=makeQuery(id+"F7.boolean.opBoolean","COPY",FACE,{"derivedFrom":makeQuery(id+"F7.opExtrude","SWEPT_FACE",FACE,{"disambiguationData":[OSD([sQuery(id+"F6.wireOp",EDGE,"E5.right")])]})});Q8=makeQuery(id+"F19.boolean.opBoolean","INTERSECT",EDGE,{"derivedFrom":[makeQuery(id+"F17.boolean.opBoolean","MERGE",FACE,{"derivedFrom":[makeQuery(id+"F16.boolean.opBoolean","COPY",FACE,{"disambiguationData":[TD([subQ23])],"derivedFrom":subQ16}),makeQuery(id+"F16.boolean.opBoolean","COPY",FACE,{"disambiguationData":[TD([subQ21])],"derivedFrom":subQ16}),makeQuery(id+"F16.boolean.opBoolean","COPY",FACE,{"disambiguationData":[TD([subQ18])],"derivedFrom":subQ16}),makeQuery(id+"F16.boolean.opBoolean","COPY",FACE,{"disambiguationData":[TD([subQ4])],"derivedFrom":subQ16})],"fromTools":[makeQuery(id+"F17.opExtrude","SWEPT_FACE",FACE,{"disambiguationData":[OSD([subQ0])]})]}),makeQuery(id+"F19.opExtrude","SWEPT_FACE",FACE,{"disambiguationData":[OSD([sQuery(id+"F18.wireOp",EDGE,"E15.top")])]})]});}
            var Q9;
            {var subQ0=sQuery(id+"F15.wireOp",EDGE,"E10");var subQ4=makeQuery(id+"F7.boolean.opBoolean","COPY",FACE,{"derivedFrom":makeQuery(id+"F7.opExtrude","SWEPT_FACE",FACE,{"disambiguationData":[OSD([sQuery(id+"F6.wireOp",EDGE,"E6.left")])]})});var subQ16=makeQuery(id+"F16.opExtrude","SWEPT_FACE",FACE,{"disambiguationData":[OSD([subQ0])]});var subQ18=makeQuery(id+"F7.boolean.opBoolean","COPY",FACE,{"derivedFrom":makeQuery(id+"F7.opExtrude","SWEPT_FACE",FACE,{"disambiguationData":[OSD([sQuery(id+"F6.wireOp",EDGE,"E5.left")])]})});var subQ21=makeQuery(id+"F7.boolean.opBoolean","COPY",FACE,{"derivedFrom":makeQuery(id+"F7.opExtrude","SWEPT_FACE",FACE,{"disambiguationData":[OSD([sQuery(id+"F6.wireOp",EDGE,"E6.right")])]})});var subQ23=makeQuery(id+"F7.boolean.opBoolean","COPY",FACE,{"derivedFrom":makeQuery(id+"F7.opExtrude","SWEPT_FACE",FACE,{"disambiguationData":[OSD([sQuery(id+"F6.wireOp",EDGE,"E5.right")])]})});Q9=makeQuery(id+"F19.boolean.opBoolean","INTERSECT",EDGE,{"derivedFrom":[makeQuery(id+"F17.boolean.opBoolean","MERGE",FACE,{"derivedFrom":[makeQuery(id+"F16.boolean.opBoolean","COPY",FACE,{"disambiguationData":[TD([subQ23])],"derivedFrom":subQ16}),makeQuery(id+"F16.boolean.opBoolean","COPY",FACE,{"disambiguationData":[TD([subQ21])],"derivedFrom":subQ16}),makeQuery(id+"F16.boolean.opBoolean","COPY",FACE,{"disambiguationData":[TD([subQ18])],"derivedFrom":subQ16}),makeQuery(id+"F16.boolean.opBoolean","COPY",FACE,{"disambiguationData":[TD([subQ4])],"derivedFrom":subQ16})],"fromTools":[makeQuery(id+"F17.opExtrude","SWEPT_FACE",FACE,{"disambiguationData":[OSD([subQ0])]})]}),makeQuery(id+"F19.opExtrude","SWEPT_FACE",FACE,{"disambiguationData":[OSD([sQuery(id+"F18.wireOp",EDGE,"E16.bottom")])]})]});}
            var Q10;
            {var subQ0=sQuery(id+"F15.wireOp",EDGE,"E10");var subQ4=makeQuery(id+"F7.boolean.opBoolean","COPY",FACE,{"derivedFrom":makeQuery(id+"F7.opExtrude","SWEPT_FACE",FACE,{"disambiguationData":[OSD([sQuery(id+"F6.wireOp",EDGE,"E6.left")])]})});var subQ16=makeQuery(id+"F16.opExtrude","SWEPT_FACE",FACE,{"disambiguationData":[OSD([subQ0])]});var subQ18=makeQuery(id+"F7.boolean.opBoolean","COPY",FACE,{"derivedFrom":makeQuery(id+"F7.opExtrude","SWEPT_FACE",FACE,{"disambiguationData":[OSD([sQuery(id+"F6.wireOp",EDGE,"E5.left")])]})});var subQ21=makeQuery(id+"F7.boolean.opBoolean","COPY",FACE,{"derivedFrom":makeQuery(id+"F7.opExtrude","SWEPT_FACE",FACE,{"disambiguationData":[OSD([sQuery(id+"F6.wireOp",EDGE,"E6.right")])]})});var subQ23=makeQuery(id+"F7.boolean.opBoolean","COPY",FACE,{"derivedFrom":makeQuery(id+"F7.opExtrude","SWEPT_FACE",FACE,{"disambiguationData":[OSD([sQuery(id+"F6.wireOp",EDGE,"E5.right")])]})});Q10=makeQuery(id+"F19.boolean.opBoolean","INTERSECT",EDGE,{"derivedFrom":[makeQuery(id+"F17.boolean.opBoolean","MERGE",FACE,{"derivedFrom":[makeQuery(id+"F16.boolean.opBoolean","COPY",FACE,{"disambiguationData":[TD([subQ23])],"derivedFrom":subQ16}),makeQuery(id+"F16.boolean.opBoolean","COPY",FACE,{"disambiguationData":[TD([subQ21])],"derivedFrom":subQ16}),makeQuery(id+"F16.boolean.opBoolean","COPY",FACE,{"disambiguationData":[TD([subQ18])],"derivedFrom":subQ16}),makeQuery(id+"F16.boolean.opBoolean","COPY",FACE,{"disambiguationData":[TD([subQ4])],"derivedFrom":subQ16})],"fromTools":[makeQuery(id+"F17.opExtrude","SWEPT_FACE",FACE,{"disambiguationData":[OSD([subQ0])]})]}),makeQuery(id+"F19.opExtrude","SWEPT_FACE",FACE,{"disambiguationData":[OSD([sQuery(id+"F18.wireOp",EDGE,"9zVCXmZD-Oea0-cQnX-vFVO-Ie0IHN23vyDU.top")])]})]});}
            var Q11;
            {var subQ0=sQuery(id+"F15.wireOp",EDGE,"E10");var subQ4=makeQuery(id+"F7.boolean.opBoolean","COPY",FACE,{"derivedFrom":makeQuery(id+"F7.opExtrude","SWEPT_FACE",FACE,{"disambiguationData":[OSD([sQuery(id+"F6.wireOp",EDGE,"E6.left")])]})});var subQ16=makeQuery(id+"F16.opExtrude","SWEPT_FACE",FACE,{"disambiguationData":[OSD([subQ0])]});var subQ18=makeQuery(id+"F7.boolean.opBoolean","COPY",FACE,{"derivedFrom":makeQuery(id+"F7.opExtrude","SWEPT_FACE",FACE,{"disambiguationData":[OSD([sQuery(id+"F6.wireOp",EDGE,"E5.left")])]})});var subQ21=makeQuery(id+"F7.boolean.opBoolean","COPY",FACE,{"derivedFrom":makeQuery(id+"F7.opExtrude","SWEPT_FACE",FACE,{"disambiguationData":[OSD([sQuery(id+"F6.wireOp",EDGE,"E6.right")])]})});var subQ23=makeQuery(id+"F7.boolean.opBoolean","COPY",FACE,{"derivedFrom":makeQuery(id+"F7.opExtrude","SWEPT_FACE",FACE,{"disambiguationData":[OSD([sQuery(id+"F6.wireOp",EDGE,"E5.right")])]})});Q11=makeQuery(id+"F19.boolean.opBoolean","INTERSECT",EDGE,{"derivedFrom":[makeQuery(id+"F17.boolean.opBoolean","MERGE",FACE,{"derivedFrom":[makeQuery(id+"F16.boolean.opBoolean","COPY",FACE,{"disambiguationData":[TD([subQ23])],"derivedFrom":subQ16}),makeQuery(id+"F16.boolean.opBoolean","COPY",FACE,{"disambiguationData":[TD([subQ21])],"derivedFrom":subQ16}),makeQuery(id+"F16.boolean.opBoolean","COPY",FACE,{"disambiguationData":[TD([subQ18])],"derivedFrom":subQ16}),makeQuery(id+"F16.boolean.opBoolean","COPY",FACE,{"disambiguationData":[TD([subQ4])],"derivedFrom":subQ16})],"fromTools":[makeQuery(id+"F17.opExtrude","SWEPT_FACE",FACE,{"disambiguationData":[OSD([subQ0])]})]}),makeQuery(id+"F19.opExtrude","SWEPT_FACE",FACE,{"disambiguationData":[OSD([sQuery(id+"F18.wireOp",EDGE,"9zVCXmZD-Oea0-cQnX-vFVO-Ie0IHN23vyDU.bottom")])]})]});}
            var Q12;
            {var subQ0=sQuery(id+"F15.wireOp",EDGE,"E10");var subQ4=makeQuery(id+"F7.boolean.opBoolean","COPY",FACE,{"derivedFrom":makeQuery(id+"F7.opExtrude","SWEPT_FACE",FACE,{"disambiguationData":[OSD([sQuery(id+"F6.wireOp",EDGE,"E6.left")])]})});var subQ16=makeQuery(id+"F16.opExtrude","SWEPT_FACE",FACE,{"disambiguationData":[OSD([subQ0])]});var subQ18=makeQuery(id+"F7.boolean.opBoolean","COPY",FACE,{"derivedFrom":makeQuery(id+"F7.opExtrude","SWEPT_FACE",FACE,{"disambiguationData":[OSD([sQuery(id+"F6.wireOp",EDGE,"E5.left")])]})});var subQ21=makeQuery(id+"F7.boolean.opBoolean","COPY",FACE,{"derivedFrom":makeQuery(id+"F7.opExtrude","SWEPT_FACE",FACE,{"disambiguationData":[OSD([sQuery(id+"F6.wireOp",EDGE,"E6.right")])]})});var subQ23=makeQuery(id+"F7.boolean.opBoolean","COPY",FACE,{"derivedFrom":makeQuery(id+"F7.opExtrude","SWEPT_FACE",FACE,{"disambiguationData":[OSD([sQuery(id+"F6.wireOp",EDGE,"E5.right")])]})});Q12=makeQuery(id+"F19.boolean.opBoolean","INTERSECT",EDGE,{"derivedFrom":[makeQuery(id+"F17.boolean.opBoolean","MERGE",FACE,{"derivedFrom":[makeQuery(id+"F16.boolean.opBoolean","COPY",FACE,{"disambiguationData":[TD([subQ23])],"derivedFrom":subQ16}),makeQuery(id+"F16.boolean.opBoolean","COPY",FACE,{"disambiguationData":[TD([subQ21])],"derivedFrom":subQ16}),makeQuery(id+"F16.boolean.opBoolean","COPY",FACE,{"disambiguationData":[TD([subQ18])],"derivedFrom":subQ16}),makeQuery(id+"F16.boolean.opBoolean","COPY",FACE,{"disambiguationData":[TD([subQ4])],"derivedFrom":subQ16})],"fromTools":[makeQuery(id+"F17.opExtrude","SWEPT_FACE",FACE,{"disambiguationData":[OSD([subQ0])]})]}),makeQuery(id+"F19.opExtrude","SWEPT_FACE",FACE,{"disambiguationData":[OSD([sQuery(id+"F18.wireOp",EDGE,"E16.top")])]})]});}
            var Q13;
            {var subQ0=sQuery(id+"F15.wireOp",EDGE,"E10");var subQ4=makeQuery(id+"F7.boolean.opBoolean","COPY",FACE,{"derivedFrom":makeQuery(id+"F7.opExtrude","SWEPT_FACE",FACE,{"disambiguationData":[OSD([sQuery(id+"F6.wireOp",EDGE,"E6.left")])]})});var subQ16=makeQuery(id+"F16.opExtrude","SWEPT_FACE",FACE,{"disambiguationData":[OSD([subQ0])]});var subQ18=makeQuery(id+"F7.boolean.opBoolean","COPY",FACE,{"derivedFrom":makeQuery(id+"F7.opExtrude","SWEPT_FACE",FACE,{"disambiguationData":[OSD([sQuery(id+"F6.wireOp",EDGE,"E5.left")])]})});var subQ21=makeQuery(id+"F7.boolean.opBoolean","COPY",FACE,{"derivedFrom":makeQuery(id+"F7.opExtrude","SWEPT_FACE",FACE,{"disambiguationData":[OSD([sQuery(id+"F6.wireOp",EDGE,"E6.right")])]})});var subQ23=makeQuery(id+"F7.boolean.opBoolean","COPY",FACE,{"derivedFrom":makeQuery(id+"F7.opExtrude","SWEPT_FACE",FACE,{"disambiguationData":[OSD([sQuery(id+"F6.wireOp",EDGE,"E5.right")])]})});Q13=makeQuery(id+"F19.boolean.opBoolean","INTERSECT",EDGE,{"derivedFrom":[makeQuery(id+"F17.boolean.opBoolean","MERGE",FACE,{"derivedFrom":[makeQuery(id+"F16.boolean.opBoolean","COPY",FACE,{"disambiguationData":[TD([subQ23])],"derivedFrom":subQ16}),makeQuery(id+"F16.boolean.opBoolean","COPY",FACE,{"disambiguationData":[TD([subQ21])],"derivedFrom":subQ16}),makeQuery(id+"F16.boolean.opBoolean","COPY",FACE,{"disambiguationData":[TD([subQ18])],"derivedFrom":subQ16}),makeQuery(id+"F16.boolean.opBoolean","COPY",FACE,{"disambiguationData":[TD([subQ4])],"derivedFrom":subQ16})],"fromTools":[makeQuery(id+"F17.opExtrude","SWEPT_FACE",FACE,{"disambiguationData":[OSD([subQ0])]})]}),makeQuery(id+"F19.opExtrude","SWEPT_FACE",FACE,{"disambiguationData":[OSD([sQuery(id+"F18.wireOp",EDGE,"E15.bottom")])]})]});}
            var Q14;
            {var subQ0=sQuery(id+"F15.wireOp",EDGE,"E10");var subQ4=makeQuery(id+"F7.boolean.opBoolean","COPY",FACE,{"derivedFrom":makeQuery(id+"F7.opExtrude","SWEPT_FACE",FACE,{"disambiguationData":[OSD([sQuery(id+"F6.wireOp",EDGE,"E6.left")])]})});var subQ16=makeQuery(id+"F16.opExtrude","SWEPT_FACE",FACE,{"disambiguationData":[OSD([subQ0])]});var subQ18=makeQuery(id+"F7.boolean.opBoolean","COPY",FACE,{"derivedFrom":makeQuery(id+"F7.opExtrude","SWEPT_FACE",FACE,{"disambiguationData":[OSD([sQuery(id+"F6.wireOp",EDGE,"E5.left")])]})});var subQ21=makeQuery(id+"F7.boolean.opBoolean","COPY",FACE,{"derivedFrom":makeQuery(id+"F7.opExtrude","SWEPT_FACE",FACE,{"disambiguationData":[OSD([sQuery(id+"F6.wireOp",EDGE,"E6.right")])]})});var subQ23=makeQuery(id+"F7.boolean.opBoolean","COPY",FACE,{"derivedFrom":makeQuery(id+"F7.opExtrude","SWEPT_FACE",FACE,{"disambiguationData":[OSD([sQuery(id+"F6.wireOp",EDGE,"E5.right")])]})});Q14=makeQuery(id+"F19.boolean.opBoolean","INTERSECT",EDGE,{"derivedFrom":[makeQuery(id+"F17.boolean.opBoolean","MERGE",FACE,{"derivedFrom":[makeQuery(id+"F16.boolean.opBoolean","COPY",FACE,{"disambiguationData":[TD([subQ23])],"derivedFrom":subQ16}),makeQuery(id+"F16.boolean.opBoolean","COPY",FACE,{"disambiguationData":[TD([subQ21])],"derivedFrom":subQ16}),makeQuery(id+"F16.boolean.opBoolean","COPY",FACE,{"disambiguationData":[TD([subQ18])],"derivedFrom":subQ16}),makeQuery(id+"F16.boolean.opBoolean","COPY",FACE,{"disambiguationData":[TD([subQ4])],"derivedFrom":subQ16})],"fromTools":[makeQuery(id+"F17.opExtrude","SWEPT_FACE",FACE,{"disambiguationData":[OSD([subQ0])]})]}),makeQuery(id+"F19.opExtrude","SWEPT_FACE",FACE,{"disambiguationData":[OSD([sQuery(id+"F18.wireOp",EDGE,"E12.bottom")])]})]});}
            var Q15;
            {var subQ0=sQuery(id+"F15.wireOp",EDGE,"E10");var subQ4=makeQuery(id+"F7.boolean.opBoolean","COPY",FACE,{"derivedFrom":makeQuery(id+"F7.opExtrude","SWEPT_FACE",FACE,{"disambiguationData":[OSD([sQuery(id+"F6.wireOp",EDGE,"E6.left")])]})});var subQ16=makeQuery(id+"F16.opExtrude","SWEPT_FACE",FACE,{"disambiguationData":[OSD([subQ0])]});var subQ18=makeQuery(id+"F7.boolean.opBoolean","COPY",FACE,{"derivedFrom":makeQuery(id+"F7.opExtrude","SWEPT_FACE",FACE,{"disambiguationData":[OSD([sQuery(id+"F6.wireOp",EDGE,"E5.left")])]})});var subQ21=makeQuery(id+"F7.boolean.opBoolean","COPY",FACE,{"derivedFrom":makeQuery(id+"F7.opExtrude","SWEPT_FACE",FACE,{"disambiguationData":[OSD([sQuery(id+"F6.wireOp",EDGE,"E6.right")])]})});var subQ23=makeQuery(id+"F7.boolean.opBoolean","COPY",FACE,{"derivedFrom":makeQuery(id+"F7.opExtrude","SWEPT_FACE",FACE,{"disambiguationData":[OSD([sQuery(id+"F6.wireOp",EDGE,"E5.right")])]})});Q15=makeQuery(id+"F19.boolean.opBoolean","INTERSECT",EDGE,{"derivedFrom":[makeQuery(id+"F17.boolean.opBoolean","MERGE",FACE,{"derivedFrom":[makeQuery(id+"F16.boolean.opBoolean","COPY",FACE,{"disambiguationData":[TD([subQ23])],"derivedFrom":subQ16}),makeQuery(id+"F16.boolean.opBoolean","COPY",FACE,{"disambiguationData":[TD([subQ21])],"derivedFrom":subQ16}),makeQuery(id+"F16.boolean.opBoolean","COPY",FACE,{"disambiguationData":[TD([subQ18])],"derivedFrom":subQ16}),makeQuery(id+"F16.boolean.opBoolean","COPY",FACE,{"disambiguationData":[TD([subQ4])],"derivedFrom":subQ16})],"fromTools":[makeQuery(id+"F17.opExtrude","SWEPT_FACE",FACE,{"disambiguationData":[OSD([subQ0])]})]}),makeQuery(id+"F19.opExtrude","SWEPT_FACE",FACE,{"disambiguationData":[OSD([sQuery(id+"F18.wireOp",EDGE,"E13.bottom")])]})]});}
            var Q16;
            {var subQ0=sQuery(id+"F15.wireOp",EDGE,"E10");var subQ4=makeQuery(id+"F7.boolean.opBoolean","COPY",FACE,{"derivedFrom":makeQuery(id+"F7.opExtrude","SWEPT_FACE",FACE,{"disambiguationData":[OSD([sQuery(id+"F6.wireOp",EDGE,"E6.left")])]})});var subQ16=makeQuery(id+"F16.opExtrude","SWEPT_FACE",FACE,{"disambiguationData":[OSD([subQ0])]});var subQ18=makeQuery(id+"F7.boolean.opBoolean","COPY",FACE,{"derivedFrom":makeQuery(id+"F7.opExtrude","SWEPT_FACE",FACE,{"disambiguationData":[OSD([sQuery(id+"F6.wireOp",EDGE,"E5.left")])]})});var subQ21=makeQuery(id+"F7.boolean.opBoolean","COPY",FACE,{"derivedFrom":makeQuery(id+"F7.opExtrude","SWEPT_FACE",FACE,{"disambiguationData":[OSD([sQuery(id+"F6.wireOp",EDGE,"E6.right")])]})});var subQ23=makeQuery(id+"F7.boolean.opBoolean","COPY",FACE,{"derivedFrom":makeQuery(id+"F7.opExtrude","SWEPT_FACE",FACE,{"disambiguationData":[OSD([sQuery(id+"F6.wireOp",EDGE,"E5.right")])]})});Q16=makeQuery(id+"F19.boolean.opBoolean","INTERSECT",EDGE,{"derivedFrom":[makeQuery(id+"F17.boolean.opBoolean","MERGE",FACE,{"derivedFrom":[makeQuery(id+"F16.boolean.opBoolean","COPY",FACE,{"disambiguationData":[TD([subQ23])],"derivedFrom":subQ16}),makeQuery(id+"F16.boolean.opBoolean","COPY",FACE,{"disambiguationData":[TD([subQ21])],"derivedFrom":subQ16}),makeQuery(id+"F16.boolean.opBoolean","COPY",FACE,{"disambiguationData":[TD([subQ18])],"derivedFrom":subQ16}),makeQuery(id+"F16.boolean.opBoolean","COPY",FACE,{"disambiguationData":[TD([subQ4])],"derivedFrom":subQ16})],"fromTools":[makeQuery(id+"F17.opExtrude","SWEPT_FACE",FACE,{"disambiguationData":[OSD([subQ0])]})]}),makeQuery(id+"F19.opExtrude","SWEPT_FACE",FACE,{"disambiguationData":[OSD([sQuery(id+"F18.wireOp",EDGE,"E14.bottom")])]})]});}
            var Q17;
            {var subQ0=sQuery(id+"F15.wireOp",EDGE,"E10");var subQ4=makeQuery(id+"F7.boolean.opBoolean","COPY",FACE,{"derivedFrom":makeQuery(id+"F7.opExtrude","SWEPT_FACE",FACE,{"disambiguationData":[OSD([sQuery(id+"F6.wireOp",EDGE,"E6.left")])]})});var subQ16=makeQuery(id+"F16.opExtrude","SWEPT_FACE",FACE,{"disambiguationData":[OSD([subQ0])]});var subQ18=makeQuery(id+"F7.boolean.opBoolean","COPY",FACE,{"derivedFrom":makeQuery(id+"F7.opExtrude","SWEPT_FACE",FACE,{"disambiguationData":[OSD([sQuery(id+"F6.wireOp",EDGE,"E5.left")])]})});var subQ21=makeQuery(id+"F7.boolean.opBoolean","COPY",FACE,{"derivedFrom":makeQuery(id+"F7.opExtrude","SWEPT_FACE",FACE,{"disambiguationData":[OSD([sQuery(id+"F6.wireOp",EDGE,"E6.right")])]})});var subQ23=makeQuery(id+"F7.boolean.opBoolean","COPY",FACE,{"derivedFrom":makeQuery(id+"F7.opExtrude","SWEPT_FACE",FACE,{"disambiguationData":[OSD([sQuery(id+"F6.wireOp",EDGE,"E5.right")])]})});Q17=makeQuery(id+"F19.boolean.opBoolean","INTERSECT",EDGE,{"derivedFrom":[makeQuery(id+"F17.boolean.opBoolean","MERGE",FACE,{"derivedFrom":[makeQuery(id+"F16.boolean.opBoolean","COPY",FACE,{"disambiguationData":[TD([subQ23])],"derivedFrom":subQ16}),makeQuery(id+"F16.boolean.opBoolean","COPY",FACE,{"disambiguationData":[TD([subQ21])],"derivedFrom":subQ16}),makeQuery(id+"F16.boolean.opBoolean","COPY",FACE,{"disambiguationData":[TD([subQ18])],"derivedFrom":subQ16}),makeQuery(id+"F16.boolean.opBoolean","COPY",FACE,{"disambiguationData":[TD([subQ4])],"derivedFrom":subQ16})],"fromTools":[makeQuery(id+"F17.opExtrude","SWEPT_FACE",FACE,{"disambiguationData":[OSD([subQ0])]})]}),makeQuery(id+"F19.opExtrude","SWEPT_FACE",FACE,{"disambiguationData":[OSD([sQuery(id+"F18.wireOp",EDGE,"3WnHr87n-zB70-hSeO-Aol3-sTKqONvJ2aJL.bottom")])]})]});}
            var Q18;
            {var subQ0=sQuery(id+"F15.wireOp",EDGE,"E10");var subQ4=makeQuery(id+"F7.boolean.opBoolean","COPY",FACE,{"derivedFrom":makeQuery(id+"F7.opExtrude","SWEPT_FACE",FACE,{"disambiguationData":[OSD([sQuery(id+"F6.wireOp",EDGE,"E6.left")])]})});var subQ16=makeQuery(id+"F16.opExtrude","SWEPT_FACE",FACE,{"disambiguationData":[OSD([subQ0])]});var subQ18=makeQuery(id+"F7.boolean.opBoolean","COPY",FACE,{"derivedFrom":makeQuery(id+"F7.opExtrude","SWEPT_FACE",FACE,{"disambiguationData":[OSD([sQuery(id+"F6.wireOp",EDGE,"E5.left")])]})});var subQ21=makeQuery(id+"F7.boolean.opBoolean","COPY",FACE,{"derivedFrom":makeQuery(id+"F7.opExtrude","SWEPT_FACE",FACE,{"disambiguationData":[OSD([sQuery(id+"F6.wireOp",EDGE,"E6.right")])]})});var subQ23=makeQuery(id+"F7.boolean.opBoolean","COPY",FACE,{"derivedFrom":makeQuery(id+"F7.opExtrude","SWEPT_FACE",FACE,{"disambiguationData":[OSD([sQuery(id+"F6.wireOp",EDGE,"E5.right")])]})});Q18=makeQuery(id+"F19.boolean.opBoolean","INTERSECT",EDGE,{"derivedFrom":[makeQuery(id+"F17.boolean.opBoolean","MERGE",FACE,{"derivedFrom":[makeQuery(id+"F16.boolean.opBoolean","COPY",FACE,{"disambiguationData":[TD([subQ23])],"derivedFrom":subQ16}),makeQuery(id+"F16.boolean.opBoolean","COPY",FACE,{"disambiguationData":[TD([subQ21])],"derivedFrom":subQ16}),makeQuery(id+"F16.boolean.opBoolean","COPY",FACE,{"disambiguationData":[TD([subQ18])],"derivedFrom":subQ16}),makeQuery(id+"F16.boolean.opBoolean","COPY",FACE,{"disambiguationData":[TD([subQ4])],"derivedFrom":subQ16})],"fromTools":[makeQuery(id+"F17.opExtrude","SWEPT_FACE",FACE,{"disambiguationData":[OSD([subQ0])]})]}),makeQuery(id+"F19.opExtrude","SWEPT_FACE",FACE,{"disambiguationData":[OSD([sQuery(id+"F18.wireOp",EDGE,"bdn7c9yY-9ESb-mA8W-PJno-jlEChpIoJOdE.bottom")])]})]});}
            var Q19;
            {var subQ0=sQuery(id+"F15.wireOp",EDGE,"E10");var subQ4=makeQuery(id+"F7.boolean.opBoolean","COPY",FACE,{"derivedFrom":makeQuery(id+"F7.opExtrude","SWEPT_FACE",FACE,{"disambiguationData":[OSD([sQuery(id+"F6.wireOp",EDGE,"E6.left")])]})});var subQ16=makeQuery(id+"F16.opExtrude","SWEPT_FACE",FACE,{"disambiguationData":[OSD([subQ0])]});var subQ18=makeQuery(id+"F7.boolean.opBoolean","COPY",FACE,{"derivedFrom":makeQuery(id+"F7.opExtrude","SWEPT_FACE",FACE,{"disambiguationData":[OSD([sQuery(id+"F6.wireOp",EDGE,"E5.left")])]})});var subQ21=makeQuery(id+"F7.boolean.opBoolean","COPY",FACE,{"derivedFrom":makeQuery(id+"F7.opExtrude","SWEPT_FACE",FACE,{"disambiguationData":[OSD([sQuery(id+"F6.wireOp",EDGE,"E6.right")])]})});var subQ23=makeQuery(id+"F7.boolean.opBoolean","COPY",FACE,{"derivedFrom":makeQuery(id+"F7.opExtrude","SWEPT_FACE",FACE,{"disambiguationData":[OSD([sQuery(id+"F6.wireOp",EDGE,"E5.right")])]})});Q19=makeQuery(id+"F19.boolean.opBoolean","INTERSECT",EDGE,{"derivedFrom":[makeQuery(id+"F17.boolean.opBoolean","MERGE",FACE,{"derivedFrom":[makeQuery(id+"F16.boolean.opBoolean","COPY",FACE,{"disambiguationData":[TD([subQ23])],"derivedFrom":subQ16}),makeQuery(id+"F16.boolean.opBoolean","COPY",FACE,{"disambiguationData":[TD([subQ21])],"derivedFrom":subQ16}),makeQuery(id+"F16.boolean.opBoolean","COPY",FACE,{"disambiguationData":[TD([subQ18])],"derivedFrom":subQ16}),makeQuery(id+"F16.boolean.opBoolean","COPY",FACE,{"disambiguationData":[TD([subQ4])],"derivedFrom":subQ16})],"fromTools":[makeQuery(id+"F17.opExtrude","SWEPT_FACE",FACE,{"disambiguationData":[OSD([subQ0])]})]}),makeQuery(id+"F19.opExtrude","SWEPT_FACE",FACE,{"disambiguationData":[OSD([sQuery(id+"F18.wireOp",EDGE,"GZ6DawBn-dVhs-ftJf-icQb-t5xCzbtVKISh.bottom")])]})]});}
            var Q20;
            {var subQ0=sQuery(id+"F15.wireOp",EDGE,"E10");var subQ4=makeQuery(id+"F7.boolean.opBoolean","COPY",FACE,{"derivedFrom":makeQuery(id+"F7.opExtrude","SWEPT_FACE",FACE,{"disambiguationData":[OSD([sQuery(id+"F6.wireOp",EDGE,"E6.left")])]})});var subQ16=makeQuery(id+"F16.opExtrude","SWEPT_FACE",FACE,{"disambiguationData":[OSD([subQ0])]});var subQ18=makeQuery(id+"F7.boolean.opBoolean","COPY",FACE,{"derivedFrom":makeQuery(id+"F7.opExtrude","SWEPT_FACE",FACE,{"disambiguationData":[OSD([sQuery(id+"F6.wireOp",EDGE,"E5.left")])]})});var subQ21=makeQuery(id+"F7.boolean.opBoolean","COPY",FACE,{"derivedFrom":makeQuery(id+"F7.opExtrude","SWEPT_FACE",FACE,{"disambiguationData":[OSD([sQuery(id+"F6.wireOp",EDGE,"E6.right")])]})});var subQ23=makeQuery(id+"F7.boolean.opBoolean","COPY",FACE,{"derivedFrom":makeQuery(id+"F7.opExtrude","SWEPT_FACE",FACE,{"disambiguationData":[OSD([sQuery(id+"F6.wireOp",EDGE,"E5.right")])]})});Q20=makeQuery(id+"F19.boolean.opBoolean","INTERSECT",EDGE,{"derivedFrom":[makeQuery(id+"F17.boolean.opBoolean","MERGE",FACE,{"derivedFrom":[makeQuery(id+"F16.boolean.opBoolean","COPY",FACE,{"disambiguationData":[TD([subQ23])],"derivedFrom":subQ16}),makeQuery(id+"F16.boolean.opBoolean","COPY",FACE,{"disambiguationData":[TD([subQ21])],"derivedFrom":subQ16}),makeQuery(id+"F16.boolean.opBoolean","COPY",FACE,{"disambiguationData":[TD([subQ18])],"derivedFrom":subQ16}),makeQuery(id+"F16.boolean.opBoolean","COPY",FACE,{"disambiguationData":[TD([subQ4])],"derivedFrom":subQ16})],"fromTools":[makeQuery(id+"F17.opExtrude","SWEPT_FACE",FACE,{"disambiguationData":[OSD([subQ0])]})]}),makeQuery(id+"F19.opExtrude","SWEPT_FACE",FACE,{"disambiguationData":[OSD([sQuery(id+"F18.wireOp",EDGE,"GZ6DawBn-dVhs-ftJf-icQb-t5xCzbtVKISh.left")])]})]});}
            var Q21;
            {var subQ0=sQuery(id+"F15.wireOp",EDGE,"E10");var subQ4=makeQuery(id+"F7.boolean.opBoolean","COPY",FACE,{"derivedFrom":makeQuery(id+"F7.opExtrude","SWEPT_FACE",FACE,{"disambiguationData":[OSD([sQuery(id+"F6.wireOp",EDGE,"E6.left")])]})});var subQ16=makeQuery(id+"F16.opExtrude","SWEPT_FACE",FACE,{"disambiguationData":[OSD([subQ0])]});var subQ18=makeQuery(id+"F7.boolean.opBoolean","COPY",FACE,{"derivedFrom":makeQuery(id+"F7.opExtrude","SWEPT_FACE",FACE,{"disambiguationData":[OSD([sQuery(id+"F6.wireOp",EDGE,"E5.left")])]})});var subQ21=makeQuery(id+"F7.boolean.opBoolean","COPY",FACE,{"derivedFrom":makeQuery(id+"F7.opExtrude","SWEPT_FACE",FACE,{"disambiguationData":[OSD([sQuery(id+"F6.wireOp",EDGE,"E6.right")])]})});var subQ23=makeQuery(id+"F7.boolean.opBoolean","COPY",FACE,{"derivedFrom":makeQuery(id+"F7.opExtrude","SWEPT_FACE",FACE,{"disambiguationData":[OSD([sQuery(id+"F6.wireOp",EDGE,"E5.right")])]})});Q21=makeQuery(id+"F19.boolean.opBoolean","INTERSECT",EDGE,{"derivedFrom":[makeQuery(id+"F17.boolean.opBoolean","MERGE",FACE,{"derivedFrom":[makeQuery(id+"F16.boolean.opBoolean","COPY",FACE,{"disambiguationData":[TD([subQ23])],"derivedFrom":subQ16}),makeQuery(id+"F16.boolean.opBoolean","COPY",FACE,{"disambiguationData":[TD([subQ21])],"derivedFrom":subQ16}),makeQuery(id+"F16.boolean.opBoolean","COPY",FACE,{"disambiguationData":[TD([subQ18])],"derivedFrom":subQ16}),makeQuery(id+"F16.boolean.opBoolean","COPY",FACE,{"disambiguationData":[TD([subQ4])],"derivedFrom":subQ16})],"fromTools":[makeQuery(id+"F17.opExtrude","SWEPT_FACE",FACE,{"disambiguationData":[OSD([subQ0])]})]}),makeQuery(id+"F19.opExtrude","SWEPT_FACE",FACE,{"disambiguationData":[OSD([sQuery(id+"F18.wireOp",EDGE,"bdn7c9yY-9ESb-mA8W-PJno-jlEChpIoJOdE.left")])]})]});}
            var Q22;
            {var subQ0=sQuery(id+"F15.wireOp",EDGE,"E10");var subQ4=makeQuery(id+"F7.boolean.opBoolean","COPY",FACE,{"derivedFrom":makeQuery(id+"F7.opExtrude","SWEPT_FACE",FACE,{"disambiguationData":[OSD([sQuery(id+"F6.wireOp",EDGE,"E6.left")])]})});var subQ16=makeQuery(id+"F16.opExtrude","SWEPT_FACE",FACE,{"disambiguationData":[OSD([subQ0])]});var subQ18=makeQuery(id+"F7.boolean.opBoolean","COPY",FACE,{"derivedFrom":makeQuery(id+"F7.opExtrude","SWEPT_FACE",FACE,{"disambiguationData":[OSD([sQuery(id+"F6.wireOp",EDGE,"E5.left")])]})});var subQ21=makeQuery(id+"F7.boolean.opBoolean","COPY",FACE,{"derivedFrom":makeQuery(id+"F7.opExtrude","SWEPT_FACE",FACE,{"disambiguationData":[OSD([sQuery(id+"F6.wireOp",EDGE,"E6.right")])]})});var subQ23=makeQuery(id+"F7.boolean.opBoolean","COPY",FACE,{"derivedFrom":makeQuery(id+"F7.opExtrude","SWEPT_FACE",FACE,{"disambiguationData":[OSD([sQuery(id+"F6.wireOp",EDGE,"E5.right")])]})});Q22=makeQuery(id+"F19.boolean.opBoolean","INTERSECT",EDGE,{"derivedFrom":[makeQuery(id+"F17.boolean.opBoolean","MERGE",FACE,{"derivedFrom":[makeQuery(id+"F16.boolean.opBoolean","COPY",FACE,{"disambiguationData":[TD([subQ23])],"derivedFrom":subQ16}),makeQuery(id+"F16.boolean.opBoolean","COPY",FACE,{"disambiguationData":[TD([subQ21])],"derivedFrom":subQ16}),makeQuery(id+"F16.boolean.opBoolean","COPY",FACE,{"disambiguationData":[TD([subQ18])],"derivedFrom":subQ16}),makeQuery(id+"F16.boolean.opBoolean","COPY",FACE,{"disambiguationData":[TD([subQ4])],"derivedFrom":subQ16})],"fromTools":[makeQuery(id+"F17.opExtrude","SWEPT_FACE",FACE,{"disambiguationData":[OSD([subQ0])]})]}),makeQuery(id+"F19.opExtrude","SWEPT_FACE",FACE,{"disambiguationData":[OSD([sQuery(id+"F18.wireOp",EDGE,"3WnHr87n-zB70-hSeO-Aol3-sTKqONvJ2aJL.left")])]})]});}
            var Q23;
            {var subQ0=sQuery(id+"F15.wireOp",EDGE,"E10");var subQ4=makeQuery(id+"F7.boolean.opBoolean","COPY",FACE,{"derivedFrom":makeQuery(id+"F7.opExtrude","SWEPT_FACE",FACE,{"disambiguationData":[OSD([sQuery(id+"F6.wireOp",EDGE,"E6.left")])]})});var subQ16=makeQuery(id+"F16.opExtrude","SWEPT_FACE",FACE,{"disambiguationData":[OSD([subQ0])]});var subQ18=makeQuery(id+"F7.boolean.opBoolean","COPY",FACE,{"derivedFrom":makeQuery(id+"F7.opExtrude","SWEPT_FACE",FACE,{"disambiguationData":[OSD([sQuery(id+"F6.wireOp",EDGE,"E5.left")])]})});var subQ21=makeQuery(id+"F7.boolean.opBoolean","COPY",FACE,{"derivedFrom":makeQuery(id+"F7.opExtrude","SWEPT_FACE",FACE,{"disambiguationData":[OSD([sQuery(id+"F6.wireOp",EDGE,"E6.right")])]})});var subQ23=makeQuery(id+"F7.boolean.opBoolean","COPY",FACE,{"derivedFrom":makeQuery(id+"F7.opExtrude","SWEPT_FACE",FACE,{"disambiguationData":[OSD([sQuery(id+"F6.wireOp",EDGE,"E5.right")])]})});Q23=makeQuery(id+"F19.boolean.opBoolean","INTERSECT",EDGE,{"derivedFrom":[makeQuery(id+"F17.boolean.opBoolean","MERGE",FACE,{"derivedFrom":[makeQuery(id+"F16.boolean.opBoolean","COPY",FACE,{"disambiguationData":[TD([subQ23])],"derivedFrom":subQ16}),makeQuery(id+"F16.boolean.opBoolean","COPY",FACE,{"disambiguationData":[TD([subQ21])],"derivedFrom":subQ16}),makeQuery(id+"F16.boolean.opBoolean","COPY",FACE,{"disambiguationData":[TD([subQ18])],"derivedFrom":subQ16}),makeQuery(id+"F16.boolean.opBoolean","COPY",FACE,{"disambiguationData":[TD([subQ4])],"derivedFrom":subQ16})],"fromTools":[makeQuery(id+"F17.opExtrude","SWEPT_FACE",FACE,{"disambiguationData":[OSD([subQ0])]})]}),makeQuery(id+"F19.opExtrude","SWEPT_FACE",FACE,{"disambiguationData":[OSD([sQuery(id+"F18.wireOp",EDGE,"E14.left")])]})]});}
            var Q24;
            {var subQ0=sQuery(id+"F15.wireOp",EDGE,"E10");var subQ4=makeQuery(id+"F7.boolean.opBoolean","COPY",FACE,{"derivedFrom":makeQuery(id+"F7.opExtrude","SWEPT_FACE",FACE,{"disambiguationData":[OSD([sQuery(id+"F6.wireOp",EDGE,"E6.left")])]})});var subQ16=makeQuery(id+"F16.opExtrude","SWEPT_FACE",FACE,{"disambiguationData":[OSD([subQ0])]});var subQ18=makeQuery(id+"F7.boolean.opBoolean","COPY",FACE,{"derivedFrom":makeQuery(id+"F7.opExtrude","SWEPT_FACE",FACE,{"disambiguationData":[OSD([sQuery(id+"F6.wireOp",EDGE,"E5.left")])]})});var subQ21=makeQuery(id+"F7.boolean.opBoolean","COPY",FACE,{"derivedFrom":makeQuery(id+"F7.opExtrude","SWEPT_FACE",FACE,{"disambiguationData":[OSD([sQuery(id+"F6.wireOp",EDGE,"E6.right")])]})});var subQ23=makeQuery(id+"F7.boolean.opBoolean","COPY",FACE,{"derivedFrom":makeQuery(id+"F7.opExtrude","SWEPT_FACE",FACE,{"disambiguationData":[OSD([sQuery(id+"F6.wireOp",EDGE,"E5.right")])]})});Q24=makeQuery(id+"F19.boolean.opBoolean","INTERSECT",EDGE,{"derivedFrom":[makeQuery(id+"F17.boolean.opBoolean","MERGE",FACE,{"derivedFrom":[makeQuery(id+"F16.boolean.opBoolean","COPY",FACE,{"disambiguationData":[TD([subQ23])],"derivedFrom":subQ16}),makeQuery(id+"F16.boolean.opBoolean","COPY",FACE,{"disambiguationData":[TD([subQ21])],"derivedFrom":subQ16}),makeQuery(id+"F16.boolean.opBoolean","COPY",FACE,{"disambiguationData":[TD([subQ18])],"derivedFrom":subQ16}),makeQuery(id+"F16.boolean.opBoolean","COPY",FACE,{"disambiguationData":[TD([subQ4])],"derivedFrom":subQ16})],"fromTools":[makeQuery(id+"F17.opExtrude","SWEPT_FACE",FACE,{"disambiguationData":[OSD([subQ0])]})]}),makeQuery(id+"F19.opExtrude","SWEPT_FACE",FACE,{"disambiguationData":[OSD([sQuery(id+"F18.wireOp",EDGE,"E13.left")])]})]});}
            var Q25;
            {var subQ0=sQuery(id+"F15.wireOp",EDGE,"E10");var subQ4=makeQuery(id+"F7.boolean.opBoolean","COPY",FACE,{"derivedFrom":makeQuery(id+"F7.opExtrude","SWEPT_FACE",FACE,{"disambiguationData":[OSD([sQuery(id+"F6.wireOp",EDGE,"E6.left")])]})});var subQ16=makeQuery(id+"F16.opExtrude","SWEPT_FACE",FACE,{"disambiguationData":[OSD([subQ0])]});var subQ18=makeQuery(id+"F7.boolean.opBoolean","COPY",FACE,{"derivedFrom":makeQuery(id+"F7.opExtrude","SWEPT_FACE",FACE,{"disambiguationData":[OSD([sQuery(id+"F6.wireOp",EDGE,"E5.left")])]})});var subQ21=makeQuery(id+"F7.boolean.opBoolean","COPY",FACE,{"derivedFrom":makeQuery(id+"F7.opExtrude","SWEPT_FACE",FACE,{"disambiguationData":[OSD([sQuery(id+"F6.wireOp",EDGE,"E6.right")])]})});var subQ23=makeQuery(id+"F7.boolean.opBoolean","COPY",FACE,{"derivedFrom":makeQuery(id+"F7.opExtrude","SWEPT_FACE",FACE,{"disambiguationData":[OSD([sQuery(id+"F6.wireOp",EDGE,"E5.right")])]})});Q25=makeQuery(id+"F19.boolean.opBoolean","INTERSECT",EDGE,{"derivedFrom":[makeQuery(id+"F17.boolean.opBoolean","MERGE",FACE,{"derivedFrom":[makeQuery(id+"F16.boolean.opBoolean","COPY",FACE,{"disambiguationData":[TD([subQ23])],"derivedFrom":subQ16}),makeQuery(id+"F16.boolean.opBoolean","COPY",FACE,{"disambiguationData":[TD([subQ21])],"derivedFrom":subQ16}),makeQuery(id+"F16.boolean.opBoolean","COPY",FACE,{"disambiguationData":[TD([subQ18])],"derivedFrom":subQ16}),makeQuery(id+"F16.boolean.opBoolean","COPY",FACE,{"disambiguationData":[TD([subQ4])],"derivedFrom":subQ16})],"fromTools":[makeQuery(id+"F17.opExtrude","SWEPT_FACE",FACE,{"disambiguationData":[OSD([subQ0])]})]}),makeQuery(id+"F19.opExtrude","SWEPT_FACE",FACE,{"disambiguationData":[OSD([sQuery(id+"F18.wireOp",EDGE,"E12.left")])]})]});}
            var Q26;
            {var subQ0=sQuery(id+"F15.wireOp",EDGE,"E10");var subQ4=makeQuery(id+"F7.boolean.opBoolean","COPY",FACE,{"derivedFrom":makeQuery(id+"F7.opExtrude","SWEPT_FACE",FACE,{"disambiguationData":[OSD([sQuery(id+"F6.wireOp",EDGE,"E6.left")])]})});var subQ16=makeQuery(id+"F16.opExtrude","SWEPT_FACE",FACE,{"disambiguationData":[OSD([subQ0])]});var subQ18=makeQuery(id+"F7.boolean.opBoolean","COPY",FACE,{"derivedFrom":makeQuery(id+"F7.opExtrude","SWEPT_FACE",FACE,{"disambiguationData":[OSD([sQuery(id+"F6.wireOp",EDGE,"E5.left")])]})});var subQ21=makeQuery(id+"F7.boolean.opBoolean","COPY",FACE,{"derivedFrom":makeQuery(id+"F7.opExtrude","SWEPT_FACE",FACE,{"disambiguationData":[OSD([sQuery(id+"F6.wireOp",EDGE,"E6.right")])]})});var subQ23=makeQuery(id+"F7.boolean.opBoolean","COPY",FACE,{"derivedFrom":makeQuery(id+"F7.opExtrude","SWEPT_FACE",FACE,{"disambiguationData":[OSD([sQuery(id+"F6.wireOp",EDGE,"E5.right")])]})});Q26=makeQuery(id+"F19.boolean.opBoolean","INTERSECT",EDGE,{"derivedFrom":[makeQuery(id+"F17.boolean.opBoolean","MERGE",FACE,{"derivedFrom":[makeQuery(id+"F16.boolean.opBoolean","COPY",FACE,{"disambiguationData":[TD([subQ23])],"derivedFrom":subQ16}),makeQuery(id+"F16.boolean.opBoolean","COPY",FACE,{"disambiguationData":[TD([subQ21])],"derivedFrom":subQ16}),makeQuery(id+"F16.boolean.opBoolean","COPY",FACE,{"disambiguationData":[TD([subQ18])],"derivedFrom":subQ16}),makeQuery(id+"F16.boolean.opBoolean","COPY",FACE,{"disambiguationData":[TD([subQ4])],"derivedFrom":subQ16})],"fromTools":[makeQuery(id+"F17.opExtrude","SWEPT_FACE",FACE,{"disambiguationData":[OSD([subQ0])]})]}),makeQuery(id+"F19.opExtrude","SWEPT_FACE",FACE,{"disambiguationData":[OSD([sQuery(id+"F18.wireOp",EDGE,"E15.left")])]})]});}
            var Q27;
            {var subQ0=sQuery(id+"F15.wireOp",EDGE,"E10");var subQ4=makeQuery(id+"F7.boolean.opBoolean","COPY",FACE,{"derivedFrom":makeQuery(id+"F7.opExtrude","SWEPT_FACE",FACE,{"disambiguationData":[OSD([sQuery(id+"F6.wireOp",EDGE,"E6.left")])]})});var subQ16=makeQuery(id+"F16.opExtrude","SWEPT_FACE",FACE,{"disambiguationData":[OSD([subQ0])]});var subQ18=makeQuery(id+"F7.boolean.opBoolean","COPY",FACE,{"derivedFrom":makeQuery(id+"F7.opExtrude","SWEPT_FACE",FACE,{"disambiguationData":[OSD([sQuery(id+"F6.wireOp",EDGE,"E5.left")])]})});var subQ21=makeQuery(id+"F7.boolean.opBoolean","COPY",FACE,{"derivedFrom":makeQuery(id+"F7.opExtrude","SWEPT_FACE",FACE,{"disambiguationData":[OSD([sQuery(id+"F6.wireOp",EDGE,"E6.right")])]})});var subQ23=makeQuery(id+"F7.boolean.opBoolean","COPY",FACE,{"derivedFrom":makeQuery(id+"F7.opExtrude","SWEPT_FACE",FACE,{"disambiguationData":[OSD([sQuery(id+"F6.wireOp",EDGE,"E5.right")])]})});Q27=makeQuery(id+"F19.boolean.opBoolean","INTERSECT",EDGE,{"derivedFrom":[makeQuery(id+"F17.boolean.opBoolean","MERGE",FACE,{"derivedFrom":[makeQuery(id+"F16.boolean.opBoolean","COPY",FACE,{"disambiguationData":[TD([subQ23])],"derivedFrom":subQ16}),makeQuery(id+"F16.boolean.opBoolean","COPY",FACE,{"disambiguationData":[TD([subQ21])],"derivedFrom":subQ16}),makeQuery(id+"F16.boolean.opBoolean","COPY",FACE,{"disambiguationData":[TD([subQ18])],"derivedFrom":subQ16}),makeQuery(id+"F16.boolean.opBoolean","COPY",FACE,{"disambiguationData":[TD([subQ4])],"derivedFrom":subQ16})],"fromTools":[makeQuery(id+"F17.opExtrude","SWEPT_FACE",FACE,{"disambiguationData":[OSD([subQ0])]})]}),makeQuery(id+"F19.opExtrude","SWEPT_FACE",FACE,{"disambiguationData":[OSD([sQuery(id+"F18.wireOp",EDGE,"E16.left")])]})]});}
            var Q28;
            {var subQ0=sQuery(id+"F15.wireOp",EDGE,"E10");var subQ4=makeQuery(id+"F7.boolean.opBoolean","COPY",FACE,{"derivedFrom":makeQuery(id+"F7.opExtrude","SWEPT_FACE",FACE,{"disambiguationData":[OSD([sQuery(id+"F6.wireOp",EDGE,"E6.left")])]})});var subQ16=makeQuery(id+"F16.opExtrude","SWEPT_FACE",FACE,{"disambiguationData":[OSD([subQ0])]});var subQ18=makeQuery(id+"F7.boolean.opBoolean","COPY",FACE,{"derivedFrom":makeQuery(id+"F7.opExtrude","SWEPT_FACE",FACE,{"disambiguationData":[OSD([sQuery(id+"F6.wireOp",EDGE,"E5.left")])]})});var subQ21=makeQuery(id+"F7.boolean.opBoolean","COPY",FACE,{"derivedFrom":makeQuery(id+"F7.opExtrude","SWEPT_FACE",FACE,{"disambiguationData":[OSD([sQuery(id+"F6.wireOp",EDGE,"E6.right")])]})});var subQ23=makeQuery(id+"F7.boolean.opBoolean","COPY",FACE,{"derivedFrom":makeQuery(id+"F7.opExtrude","SWEPT_FACE",FACE,{"disambiguationData":[OSD([sQuery(id+"F6.wireOp",EDGE,"E5.right")])]})});Q28=makeQuery(id+"F19.boolean.opBoolean","INTERSECT",EDGE,{"derivedFrom":[makeQuery(id+"F17.boolean.opBoolean","MERGE",FACE,{"derivedFrom":[makeQuery(id+"F16.boolean.opBoolean","COPY",FACE,{"disambiguationData":[TD([subQ23])],"derivedFrom":subQ16}),makeQuery(id+"F16.boolean.opBoolean","COPY",FACE,{"disambiguationData":[TD([subQ21])],"derivedFrom":subQ16}),makeQuery(id+"F16.boolean.opBoolean","COPY",FACE,{"disambiguationData":[TD([subQ18])],"derivedFrom":subQ16}),makeQuery(id+"F16.boolean.opBoolean","COPY",FACE,{"disambiguationData":[TD([subQ4])],"derivedFrom":subQ16})],"fromTools":[makeQuery(id+"F17.opExtrude","SWEPT_FACE",FACE,{"disambiguationData":[OSD([subQ0])]})]}),makeQuery(id+"F19.opExtrude","SWEPT_FACE",FACE,{"disambiguationData":[OSD([sQuery(id+"F18.wireOp",EDGE,"9zVCXmZD-Oea0-cQnX-vFVO-Ie0IHN23vyDU.left")])]})]});}
            var Q29;
            {var subQ0=sQuery(id+"F15.wireOp",EDGE,"E10");var subQ4=makeQuery(id+"F7.boolean.opBoolean","COPY",FACE,{"derivedFrom":makeQuery(id+"F7.opExtrude","SWEPT_FACE",FACE,{"disambiguationData":[OSD([sQuery(id+"F6.wireOp",EDGE,"E6.left")])]})});var subQ16=makeQuery(id+"F16.opExtrude","SWEPT_FACE",FACE,{"disambiguationData":[OSD([subQ0])]});var subQ18=makeQuery(id+"F7.boolean.opBoolean","COPY",FACE,{"derivedFrom":makeQuery(id+"F7.opExtrude","SWEPT_FACE",FACE,{"disambiguationData":[OSD([sQuery(id+"F6.wireOp",EDGE,"E5.left")])]})});var subQ21=makeQuery(id+"F7.boolean.opBoolean","COPY",FACE,{"derivedFrom":makeQuery(id+"F7.opExtrude","SWEPT_FACE",FACE,{"disambiguationData":[OSD([sQuery(id+"F6.wireOp",EDGE,"E6.right")])]})});var subQ23=makeQuery(id+"F7.boolean.opBoolean","COPY",FACE,{"derivedFrom":makeQuery(id+"F7.opExtrude","SWEPT_FACE",FACE,{"disambiguationData":[OSD([sQuery(id+"F6.wireOp",EDGE,"E5.right")])]})});Q29=makeQuery(id+"F19.boolean.opBoolean","INTERSECT",EDGE,{"derivedFrom":[makeQuery(id+"F17.boolean.opBoolean","MERGE",FACE,{"derivedFrom":[makeQuery(id+"F16.boolean.opBoolean","COPY",FACE,{"disambiguationData":[TD([subQ23])],"derivedFrom":subQ16}),makeQuery(id+"F16.boolean.opBoolean","COPY",FACE,{"disambiguationData":[TD([subQ21])],"derivedFrom":subQ16}),makeQuery(id+"F16.boolean.opBoolean","COPY",FACE,{"disambiguationData":[TD([subQ18])],"derivedFrom":subQ16}),makeQuery(id+"F16.boolean.opBoolean","COPY",FACE,{"disambiguationData":[TD([subQ4])],"derivedFrom":subQ16})],"fromTools":[makeQuery(id+"F17.opExtrude","SWEPT_FACE",FACE,{"disambiguationData":[OSD([subQ0])]})]}),makeQuery(id+"F19.opExtrude","SWEPT_FACE",FACE,{"disambiguationData":[OSD([sQuery(id+"F18.wireOp",EDGE,"GZ6DawBn-dVhs-ftJf-icQb-t5xCzbtVKISh.right")])]})]});}
            var Q30;
            {var subQ0=sQuery(id+"F15.wireOp",EDGE,"E10");var subQ4=makeQuery(id+"F7.boolean.opBoolean","COPY",FACE,{"derivedFrom":makeQuery(id+"F7.opExtrude","SWEPT_FACE",FACE,{"disambiguationData":[OSD([sQuery(id+"F6.wireOp",EDGE,"E6.left")])]})});var subQ16=makeQuery(id+"F16.opExtrude","SWEPT_FACE",FACE,{"disambiguationData":[OSD([subQ0])]});var subQ18=makeQuery(id+"F7.boolean.opBoolean","COPY",FACE,{"derivedFrom":makeQuery(id+"F7.opExtrude","SWEPT_FACE",FACE,{"disambiguationData":[OSD([sQuery(id+"F6.wireOp",EDGE,"E5.left")])]})});var subQ21=makeQuery(id+"F7.boolean.opBoolean","COPY",FACE,{"derivedFrom":makeQuery(id+"F7.opExtrude","SWEPT_FACE",FACE,{"disambiguationData":[OSD([sQuery(id+"F6.wireOp",EDGE,"E6.right")])]})});var subQ23=makeQuery(id+"F7.boolean.opBoolean","COPY",FACE,{"derivedFrom":makeQuery(id+"F7.opExtrude","SWEPT_FACE",FACE,{"disambiguationData":[OSD([sQuery(id+"F6.wireOp",EDGE,"E5.right")])]})});Q30=makeQuery(id+"F19.boolean.opBoolean","INTERSECT",EDGE,{"derivedFrom":[makeQuery(id+"F17.boolean.opBoolean","MERGE",FACE,{"derivedFrom":[makeQuery(id+"F16.boolean.opBoolean","COPY",FACE,{"disambiguationData":[TD([subQ23])],"derivedFrom":subQ16}),makeQuery(id+"F16.boolean.opBoolean","COPY",FACE,{"disambiguationData":[TD([subQ21])],"derivedFrom":subQ16}),makeQuery(id+"F16.boolean.opBoolean","COPY",FACE,{"disambiguationData":[TD([subQ18])],"derivedFrom":subQ16}),makeQuery(id+"F16.boolean.opBoolean","COPY",FACE,{"disambiguationData":[TD([subQ4])],"derivedFrom":subQ16})],"fromTools":[makeQuery(id+"F17.opExtrude","SWEPT_FACE",FACE,{"disambiguationData":[OSD([subQ0])]})]}),makeQuery(id+"F19.opExtrude","SWEPT_FACE",FACE,{"disambiguationData":[OSD([sQuery(id+"F18.wireOp",EDGE,"bdn7c9yY-9ESb-mA8W-PJno-jlEChpIoJOdE.right")])]})]});}
            var Q31;
            {var subQ0=sQuery(id+"F15.wireOp",EDGE,"E10");var subQ4=makeQuery(id+"F7.boolean.opBoolean","COPY",FACE,{"derivedFrom":makeQuery(id+"F7.opExtrude","SWEPT_FACE",FACE,{"disambiguationData":[OSD([sQuery(id+"F6.wireOp",EDGE,"E6.left")])]})});var subQ16=makeQuery(id+"F16.opExtrude","SWEPT_FACE",FACE,{"disambiguationData":[OSD([subQ0])]});var subQ18=makeQuery(id+"F7.boolean.opBoolean","COPY",FACE,{"derivedFrom":makeQuery(id+"F7.opExtrude","SWEPT_FACE",FACE,{"disambiguationData":[OSD([sQuery(id+"F6.wireOp",EDGE,"E5.left")])]})});var subQ21=makeQuery(id+"F7.boolean.opBoolean","COPY",FACE,{"derivedFrom":makeQuery(id+"F7.opExtrude","SWEPT_FACE",FACE,{"disambiguationData":[OSD([sQuery(id+"F6.wireOp",EDGE,"E6.right")])]})});var subQ23=makeQuery(id+"F7.boolean.opBoolean","COPY",FACE,{"derivedFrom":makeQuery(id+"F7.opExtrude","SWEPT_FACE",FACE,{"disambiguationData":[OSD([sQuery(id+"F6.wireOp",EDGE,"E5.right")])]})});Q31=makeQuery(id+"F19.boolean.opBoolean","INTERSECT",EDGE,{"derivedFrom":[makeQuery(id+"F17.boolean.opBoolean","MERGE",FACE,{"derivedFrom":[makeQuery(id+"F16.boolean.opBoolean","COPY",FACE,{"disambiguationData":[TD([subQ23])],"derivedFrom":subQ16}),makeQuery(id+"F16.boolean.opBoolean","COPY",FACE,{"disambiguationData":[TD([subQ21])],"derivedFrom":subQ16}),makeQuery(id+"F16.boolean.opBoolean","COPY",FACE,{"disambiguationData":[TD([subQ18])],"derivedFrom":subQ16}),makeQuery(id+"F16.boolean.opBoolean","COPY",FACE,{"disambiguationData":[TD([subQ4])],"derivedFrom":subQ16})],"fromTools":[makeQuery(id+"F17.opExtrude","SWEPT_FACE",FACE,{"disambiguationData":[OSD([subQ0])]})]}),makeQuery(id+"F19.opExtrude","SWEPT_FACE",FACE,{"disambiguationData":[OSD([sQuery(id+"F18.wireOp",EDGE,"3WnHr87n-zB70-hSeO-Aol3-sTKqONvJ2aJL.right")])]})]});}
            var Q32;
            {var subQ0=sQuery(id+"F15.wireOp",EDGE,"E10");var subQ4=makeQuery(id+"F7.boolean.opBoolean","COPY",FACE,{"derivedFrom":makeQuery(id+"F7.opExtrude","SWEPT_FACE",FACE,{"disambiguationData":[OSD([sQuery(id+"F6.wireOp",EDGE,"E6.left")])]})});var subQ16=makeQuery(id+"F16.opExtrude","SWEPT_FACE",FACE,{"disambiguationData":[OSD([subQ0])]});var subQ18=makeQuery(id+"F7.boolean.opBoolean","COPY",FACE,{"derivedFrom":makeQuery(id+"F7.opExtrude","SWEPT_FACE",FACE,{"disambiguationData":[OSD([sQuery(id+"F6.wireOp",EDGE,"E5.left")])]})});var subQ21=makeQuery(id+"F7.boolean.opBoolean","COPY",FACE,{"derivedFrom":makeQuery(id+"F7.opExtrude","SWEPT_FACE",FACE,{"disambiguationData":[OSD([sQuery(id+"F6.wireOp",EDGE,"E6.right")])]})});var subQ23=makeQuery(id+"F7.boolean.opBoolean","COPY",FACE,{"derivedFrom":makeQuery(id+"F7.opExtrude","SWEPT_FACE",FACE,{"disambiguationData":[OSD([sQuery(id+"F6.wireOp",EDGE,"E5.right")])]})});Q32=makeQuery(id+"F19.boolean.opBoolean","INTERSECT",EDGE,{"derivedFrom":[makeQuery(id+"F17.boolean.opBoolean","MERGE",FACE,{"derivedFrom":[makeQuery(id+"F16.boolean.opBoolean","COPY",FACE,{"disambiguationData":[TD([subQ23])],"derivedFrom":subQ16}),makeQuery(id+"F16.boolean.opBoolean","COPY",FACE,{"disambiguationData":[TD([subQ21])],"derivedFrom":subQ16}),makeQuery(id+"F16.boolean.opBoolean","COPY",FACE,{"disambiguationData":[TD([subQ18])],"derivedFrom":subQ16}),makeQuery(id+"F16.boolean.opBoolean","COPY",FACE,{"disambiguationData":[TD([subQ4])],"derivedFrom":subQ16})],"fromTools":[makeQuery(id+"F17.opExtrude","SWEPT_FACE",FACE,{"disambiguationData":[OSD([subQ0])]})]}),makeQuery(id+"F19.opExtrude","SWEPT_FACE",FACE,{"disambiguationData":[OSD([sQuery(id+"F18.wireOp",EDGE,"E14.right")])]})]});}
            var Q33;
            {var subQ0=sQuery(id+"F15.wireOp",EDGE,"E10");var subQ4=makeQuery(id+"F7.boolean.opBoolean","COPY",FACE,{"derivedFrom":makeQuery(id+"F7.opExtrude","SWEPT_FACE",FACE,{"disambiguationData":[OSD([sQuery(id+"F6.wireOp",EDGE,"E6.left")])]})});var subQ16=makeQuery(id+"F16.opExtrude","SWEPT_FACE",FACE,{"disambiguationData":[OSD([subQ0])]});var subQ18=makeQuery(id+"F7.boolean.opBoolean","COPY",FACE,{"derivedFrom":makeQuery(id+"F7.opExtrude","SWEPT_FACE",FACE,{"disambiguationData":[OSD([sQuery(id+"F6.wireOp",EDGE,"E5.left")])]})});var subQ21=makeQuery(id+"F7.boolean.opBoolean","COPY",FACE,{"derivedFrom":makeQuery(id+"F7.opExtrude","SWEPT_FACE",FACE,{"disambiguationData":[OSD([sQuery(id+"F6.wireOp",EDGE,"E6.right")])]})});var subQ23=makeQuery(id+"F7.boolean.opBoolean","COPY",FACE,{"derivedFrom":makeQuery(id+"F7.opExtrude","SWEPT_FACE",FACE,{"disambiguationData":[OSD([sQuery(id+"F6.wireOp",EDGE,"E5.right")])]})});Q33=makeQuery(id+"F19.boolean.opBoolean","INTERSECT",EDGE,{"derivedFrom":[makeQuery(id+"F17.boolean.opBoolean","MERGE",FACE,{"derivedFrom":[makeQuery(id+"F16.boolean.opBoolean","COPY",FACE,{"disambiguationData":[TD([subQ23])],"derivedFrom":subQ16}),makeQuery(id+"F16.boolean.opBoolean","COPY",FACE,{"disambiguationData":[TD([subQ21])],"derivedFrom":subQ16}),makeQuery(id+"F16.boolean.opBoolean","COPY",FACE,{"disambiguationData":[TD([subQ18])],"derivedFrom":subQ16}),makeQuery(id+"F16.boolean.opBoolean","COPY",FACE,{"disambiguationData":[TD([subQ4])],"derivedFrom":subQ16})],"fromTools":[makeQuery(id+"F17.opExtrude","SWEPT_FACE",FACE,{"disambiguationData":[OSD([subQ0])]})]}),makeQuery(id+"F19.opExtrude","SWEPT_FACE",FACE,{"disambiguationData":[OSD([sQuery(id+"F18.wireOp",EDGE,"E13.right")])]})]});}
            var Q34;
            {var subQ0=sQuery(id+"F15.wireOp",EDGE,"E10");var subQ4=makeQuery(id+"F7.boolean.opBoolean","COPY",FACE,{"derivedFrom":makeQuery(id+"F7.opExtrude","SWEPT_FACE",FACE,{"disambiguationData":[OSD([sQuery(id+"F6.wireOp",EDGE,"E6.left")])]})});var subQ16=makeQuery(id+"F16.opExtrude","SWEPT_FACE",FACE,{"disambiguationData":[OSD([subQ0])]});var subQ18=makeQuery(id+"F7.boolean.opBoolean","COPY",FACE,{"derivedFrom":makeQuery(id+"F7.opExtrude","SWEPT_FACE",FACE,{"disambiguationData":[OSD([sQuery(id+"F6.wireOp",EDGE,"E5.left")])]})});var subQ21=makeQuery(id+"F7.boolean.opBoolean","COPY",FACE,{"derivedFrom":makeQuery(id+"F7.opExtrude","SWEPT_FACE",FACE,{"disambiguationData":[OSD([sQuery(id+"F6.wireOp",EDGE,"E6.right")])]})});var subQ23=makeQuery(id+"F7.boolean.opBoolean","COPY",FACE,{"derivedFrom":makeQuery(id+"F7.opExtrude","SWEPT_FACE",FACE,{"disambiguationData":[OSD([sQuery(id+"F6.wireOp",EDGE,"E5.right")])]})});Q34=makeQuery(id+"F19.boolean.opBoolean","INTERSECT",EDGE,{"derivedFrom":[makeQuery(id+"F17.boolean.opBoolean","MERGE",FACE,{"derivedFrom":[makeQuery(id+"F16.boolean.opBoolean","COPY",FACE,{"disambiguationData":[TD([subQ23])],"derivedFrom":subQ16}),makeQuery(id+"F16.boolean.opBoolean","COPY",FACE,{"disambiguationData":[TD([subQ21])],"derivedFrom":subQ16}),makeQuery(id+"F16.boolean.opBoolean","COPY",FACE,{"disambiguationData":[TD([subQ18])],"derivedFrom":subQ16}),makeQuery(id+"F16.boolean.opBoolean","COPY",FACE,{"disambiguationData":[TD([subQ4])],"derivedFrom":subQ16})],"fromTools":[makeQuery(id+"F17.opExtrude","SWEPT_FACE",FACE,{"disambiguationData":[OSD([subQ0])]})]}),makeQuery(id+"F19.opExtrude","SWEPT_FACE",FACE,{"disambiguationData":[OSD([sQuery(id+"F18.wireOp",EDGE,"E12.right")])]})]});}
            var Q35;
            {var subQ0=sQuery(id+"F15.wireOp",EDGE,"E10");var subQ4=makeQuery(id+"F7.boolean.opBoolean","COPY",FACE,{"derivedFrom":makeQuery(id+"F7.opExtrude","SWEPT_FACE",FACE,{"disambiguationData":[OSD([sQuery(id+"F6.wireOp",EDGE,"E6.left")])]})});var subQ16=makeQuery(id+"F16.opExtrude","SWEPT_FACE",FACE,{"disambiguationData":[OSD([subQ0])]});var subQ18=makeQuery(id+"F7.boolean.opBoolean","COPY",FACE,{"derivedFrom":makeQuery(id+"F7.opExtrude","SWEPT_FACE",FACE,{"disambiguationData":[OSD([sQuery(id+"F6.wireOp",EDGE,"E5.left")])]})});var subQ21=makeQuery(id+"F7.boolean.opBoolean","COPY",FACE,{"derivedFrom":makeQuery(id+"F7.opExtrude","SWEPT_FACE",FACE,{"disambiguationData":[OSD([sQuery(id+"F6.wireOp",EDGE,"E6.right")])]})});var subQ23=makeQuery(id+"F7.boolean.opBoolean","COPY",FACE,{"derivedFrom":makeQuery(id+"F7.opExtrude","SWEPT_FACE",FACE,{"disambiguationData":[OSD([sQuery(id+"F6.wireOp",EDGE,"E5.right")])]})});Q35=makeQuery(id+"F19.boolean.opBoolean","INTERSECT",EDGE,{"derivedFrom":[makeQuery(id+"F17.boolean.opBoolean","MERGE",FACE,{"derivedFrom":[makeQuery(id+"F16.boolean.opBoolean","COPY",FACE,{"disambiguationData":[TD([subQ23])],"derivedFrom":subQ16}),makeQuery(id+"F16.boolean.opBoolean","COPY",FACE,{"disambiguationData":[TD([subQ21])],"derivedFrom":subQ16}),makeQuery(id+"F16.boolean.opBoolean","COPY",FACE,{"disambiguationData":[TD([subQ18])],"derivedFrom":subQ16}),makeQuery(id+"F16.boolean.opBoolean","COPY",FACE,{"disambiguationData":[TD([subQ4])],"derivedFrom":subQ16})],"fromTools":[makeQuery(id+"F17.opExtrude","SWEPT_FACE",FACE,{"disambiguationData":[OSD([subQ0])]})]}),makeQuery(id+"F19.opExtrude","SWEPT_FACE",FACE,{"disambiguationData":[OSD([sQuery(id+"F18.wireOp",EDGE,"E15.right")])]})]});}
            var Q36;
            {var subQ0=sQuery(id+"F15.wireOp",EDGE,"E10");var subQ4=makeQuery(id+"F7.boolean.opBoolean","COPY",FACE,{"derivedFrom":makeQuery(id+"F7.opExtrude","SWEPT_FACE",FACE,{"disambiguationData":[OSD([sQuery(id+"F6.wireOp",EDGE,"E6.left")])]})});var subQ16=makeQuery(id+"F16.opExtrude","SWEPT_FACE",FACE,{"disambiguationData":[OSD([subQ0])]});var subQ18=makeQuery(id+"F7.boolean.opBoolean","COPY",FACE,{"derivedFrom":makeQuery(id+"F7.opExtrude","SWEPT_FACE",FACE,{"disambiguationData":[OSD([sQuery(id+"F6.wireOp",EDGE,"E5.left")])]})});var subQ21=makeQuery(id+"F7.boolean.opBoolean","COPY",FACE,{"derivedFrom":makeQuery(id+"F7.opExtrude","SWEPT_FACE",FACE,{"disambiguationData":[OSD([sQuery(id+"F6.wireOp",EDGE,"E6.right")])]})});var subQ23=makeQuery(id+"F7.boolean.opBoolean","COPY",FACE,{"derivedFrom":makeQuery(id+"F7.opExtrude","SWEPT_FACE",FACE,{"disambiguationData":[OSD([sQuery(id+"F6.wireOp",EDGE,"E5.right")])]})});Q36=makeQuery(id+"F19.boolean.opBoolean","INTERSECT",EDGE,{"derivedFrom":[makeQuery(id+"F17.boolean.opBoolean","MERGE",FACE,{"derivedFrom":[makeQuery(id+"F16.boolean.opBoolean","COPY",FACE,{"disambiguationData":[TD([subQ23])],"derivedFrom":subQ16}),makeQuery(id+"F16.boolean.opBoolean","COPY",FACE,{"disambiguationData":[TD([subQ21])],"derivedFrom":subQ16}),makeQuery(id+"F16.boolean.opBoolean","COPY",FACE,{"disambiguationData":[TD([subQ18])],"derivedFrom":subQ16}),makeQuery(id+"F16.boolean.opBoolean","COPY",FACE,{"disambiguationData":[TD([subQ4])],"derivedFrom":subQ16})],"fromTools":[makeQuery(id+"F17.opExtrude","SWEPT_FACE",FACE,{"disambiguationData":[OSD([subQ0])]})]}),makeQuery(id+"F19.opExtrude","SWEPT_FACE",FACE,{"disambiguationData":[OSD([sQuery(id+"F18.wireOp",EDGE,"E16.right")])]})]});}
            var Q37;
            {var subQ0=sQuery(id+"F15.wireOp",EDGE,"E10");var subQ4=makeQuery(id+"F7.boolean.opBoolean","COPY",FACE,{"derivedFrom":makeQuery(id+"F7.opExtrude","SWEPT_FACE",FACE,{"disambiguationData":[OSD([sQuery(id+"F6.wireOp",EDGE,"E6.left")])]})});var subQ16=makeQuery(id+"F16.opExtrude","SWEPT_FACE",FACE,{"disambiguationData":[OSD([subQ0])]});var subQ18=makeQuery(id+"F7.boolean.opBoolean","COPY",FACE,{"derivedFrom":makeQuery(id+"F7.opExtrude","SWEPT_FACE",FACE,{"disambiguationData":[OSD([sQuery(id+"F6.wireOp",EDGE,"E5.left")])]})});var subQ21=makeQuery(id+"F7.boolean.opBoolean","COPY",FACE,{"derivedFrom":makeQuery(id+"F7.opExtrude","SWEPT_FACE",FACE,{"disambiguationData":[OSD([sQuery(id+"F6.wireOp",EDGE,"E6.right")])]})});var subQ23=makeQuery(id+"F7.boolean.opBoolean","COPY",FACE,{"derivedFrom":makeQuery(id+"F7.opExtrude","SWEPT_FACE",FACE,{"disambiguationData":[OSD([sQuery(id+"F6.wireOp",EDGE,"E5.right")])]})});Q37=makeQuery(id+"F19.boolean.opBoolean","INTERSECT",EDGE,{"derivedFrom":[makeQuery(id+"F17.boolean.opBoolean","MERGE",FACE,{"derivedFrom":[makeQuery(id+"F16.boolean.opBoolean","COPY",FACE,{"disambiguationData":[TD([subQ23])],"derivedFrom":subQ16}),makeQuery(id+"F16.boolean.opBoolean","COPY",FACE,{"disambiguationData":[TD([subQ21])],"derivedFrom":subQ16}),makeQuery(id+"F16.boolean.opBoolean","COPY",FACE,{"disambiguationData":[TD([subQ18])],"derivedFrom":subQ16}),makeQuery(id+"F16.boolean.opBoolean","COPY",FACE,{"disambiguationData":[TD([subQ4])],"derivedFrom":subQ16})],"fromTools":[makeQuery(id+"F17.opExtrude","SWEPT_FACE",FACE,{"disambiguationData":[OSD([subQ0])]})]}),makeQuery(id+"F19.opExtrude","SWEPT_FACE",FACE,{"disambiguationData":[OSD([sQuery(id+"F18.wireOp",EDGE,"9zVCXmZD-Oea0-cQnX-vFVO-Ie0IHN23vyDU.right")])]})]});}
            fillet(context, id + "F22", {"entities" : qUnion([Q0, Q1, Q2, Q3, Q4, Q5, Q6, Q7, Q8, Q9, Q10, Q11, Q12, Q13, Q14, Q15, Q16, Q17, Q18, Q19, Q20, Q21, Q22, Q23, Q24, Q25, Q26, Q27, Q28, Q29, Q30, Q31, Q32, Q33, Q34, Q35, Q36, Q37]), "radius" : 0.1 * mm, "tangentPropagation" : true, "allowEdgeOverflow" : false});
        }
        {
            var Q0;
            Q0=makeQuery(id+"F17.boolean.opBoolean","INTERSECT",EDGE,{"derivedFrom":[makeQuery(id+"F8.opFillet","BLEND_FACE",FACE,{"disambiguationData":[OSD([sQuery(id+"F4.wireOp",EDGE,"E3.bottom"),sQuery(id+"F4.wireOp",EDGE,"E3.right")])]}),makeQuery(id+"F17.opExtrude","SWEPT_FACE",FACE,{"disambiguationData":[OSD([sQuery(id+"F15.wireOp",EDGE,"E10")])]})]});
            var Q1;
            Q1=makeQuery(id+"F17.boolean.opBoolean","INTERSECT",EDGE,{"derivedFrom":[makeQuery(id+"F8.opFillet","BLEND_FACE",FACE,{"disambiguationData":[OSD([sQuery(id+"F4.wireOp",EDGE,"E2.top"),sQuery(id+"F4.wireOp",EDGE,"E2.right")])]}),makeQuery(id+"F17.opExtrude","SWEPT_FACE",FACE,{"disambiguationData":[OSD([sQuery(id+"F15.wireOp",EDGE,"E10")])]})]});
            var Q2;
            Q2=makeQuery(id+"F14.boolean.opBoolean","INTERSECT",EDGE,{"derivedFrom":[makeQuery(id+"F7.boolean.opBoolean","SPLIT",FACE,{"disambiguationData":[TD([makeQuery(id+"F5.boolean.opBoolean","COPY",FACE,{"derivedFrom":makeQuery(id+"F5.opExtrude","SWEPT_FACE",FACE,{"disambiguationData":[OSD([sQuery(id+"F4.wireOp",EDGE,"E3.right")])]})})])],"derivedFrom":makeQuery(id+"F5.boolean.opBoolean","COPY",FACE,{"derivedFrom":makeQuery(id+"F5.opExtrude","SWEPT_FACE",FACE,{"disambiguationData":[OSD([sQuery(id+"F4.wireOp",EDGE,"E3.top")])]})})}),makeQuery(id+"F14.opExtrude","SWEPT_FACE",FACE,{"disambiguationData":[OSD([sQuery(id+"F13.wireOp",EDGE,"E9")])]})]});
            var Q3;
            Q3=makeQuery(id+"F14.boolean.opBoolean","INTERSECT",EDGE,{"derivedFrom":[makeQuery(id+"F5.boolean.opBoolean","COPY",FACE,{"derivedFrom":makeQuery(id+"F5.opExtrude","SWEPT_FACE",FACE,{"disambiguationData":[OSD([sQuery(id+"F4.wireOp",EDGE,"E2.top")])]})}),makeQuery(id+"F14.opExtrude","SWEPT_FACE",FACE,{"disambiguationData":[OSD([sQuery(id+"F13.wireOp",EDGE,"E9")])]})]});
            var Q4;
            Q4=makeQuery(id+"F17.boolean.opBoolean","COPY",EDGE,{"derivedFrom":makeQuery(id+"F17.opExtrude","CAP_EDGE",EDGE,{"disambiguationData":[OSD([sQuery(id+"F15.wireOp",EDGE,"E10")])],"isStart":true})});
            var Q5;
            Q5=makeQuery(id+"F14.boolean.opBoolean","INTERSECT",EDGE,{"derivedFrom":[makeQuery(id+"F10.boolean.opBoolean","COPY",FACE,{"disambiguationData":[TD([makeQuery(id+"F7.boolean.opBoolean","COPY",FACE,{"derivedFrom":makeQuery(id+"F7.opExtrude","SWEPT_FACE",FACE,{"disambiguationData":[OSD([sQuery(id+"F6.wireOp",EDGE,"E6.left")])]})})])],"derivedFrom":makeQuery(id+"F10.opExtrude","SWEPT_FACE",FACE,{"disambiguationData":[OSD([sQuery(id+"F9.wireOp",EDGE,"E8.top")])]})}),makeQuery(id+"F14.opExtrude","SWEPT_FACE",FACE,{"disambiguationData":[OSD([sQuery(id+"F13.wireOp",EDGE,"E9")])]})]});
            var Q6;
            {var subQ0=sQuery(id+"F0.wireOp",EDGE,"E0.right");Q6=makeQuery(id+"F14.boolean.opBoolean","INTERSECT",EDGE,{"derivedFrom":[makeQuery(id+"F10.boolean.opBoolean","COPY",FACE,{"disambiguationData":[TD([makeQuery(id+"F1.opExtrude","SWEPT_FACE",FACE,{"disambiguationData":[OSD([subQ0])]})])],"derivedFrom":makeQuery(id+"F10.opExtrude","SWEPT_FACE",FACE,{"disambiguationData":[OSD([sQuery(id+"F9.wireOp",EDGE,"E8.top")])]})}),makeQuery(id+"F14.opExtrude","SWEPT_FACE",FACE,{"disambiguationData":[OSD([sQuery(id+"F13.wireOp",EDGE,"E9")])]})]});}
            var Q7;
            Q7=makeQuery(id+"F14.boolean.opBoolean","INTERSECT",EDGE,{"derivedFrom":[makeQuery(id+"F10.boolean.opBoolean","COPY",FACE,{"disambiguationData":[TD([makeQuery(id+"F7.boolean.opBoolean","COPY",FACE,{"derivedFrom":makeQuery(id+"F7.opExtrude","SWEPT_FACE",FACE,{"disambiguationData":[OSD([sQuery(id+"F6.wireOp",EDGE,"E5.left")])]})})])],"derivedFrom":makeQuery(id+"F10.opExtrude","SWEPT_FACE",FACE,{"disambiguationData":[OSD([sQuery(id+"F9.wireOp",EDGE,"E7.top")])]})}),makeQuery(id+"F14.opExtrude","SWEPT_FACE",FACE,{"disambiguationData":[OSD([sQuery(id+"F13.wireOp",EDGE,"E9")])]})]});
            var Q8;
            Q8=makeQuery(id+"F16.boolean.opBoolean","INTERSECT",EDGE,{"derivedFrom":[makeQuery(id+"F10.boolean.opBoolean","COPY",FACE,{"disambiguationData":[TD([makeQuery(id+"F7.boolean.opBoolean","COPY",FACE,{"derivedFrom":makeQuery(id+"F7.opExtrude","SWEPT_FACE",FACE,{"disambiguationData":[OSD([sQuery(id+"F6.wireOp",EDGE,"E6.left")])]})})])],"derivedFrom":makeQuery(id+"F10.opExtrude","SWEPT_FACE",FACE,{"disambiguationData":[OSD([sQuery(id+"F9.wireOp",EDGE,"E8.top")])]})}),makeQuery(id+"F16.opExtrude","SWEPT_FACE",FACE,{"disambiguationData":[OSD([sQuery(id+"F15.wireOp",EDGE,"E10")])]})]});
            var Q9;
            Q9=makeQuery(id+"F16.boolean.opBoolean","INTERSECT",EDGE,{"derivedFrom":[makeQuery(id+"F10.boolean.opBoolean","COPY",FACE,{"disambiguationData":[TD([makeQuery(id+"F7.boolean.opBoolean","COPY",FACE,{"derivedFrom":makeQuery(id+"F7.opExtrude","SWEPT_FACE",FACE,{"disambiguationData":[OSD([sQuery(id+"F6.wireOp",EDGE,"E5.left")])]})})])],"derivedFrom":makeQuery(id+"F10.opExtrude","SWEPT_FACE",FACE,{"disambiguationData":[OSD([sQuery(id+"F9.wireOp",EDGE,"E7.top")])]})}),makeQuery(id+"F16.opExtrude","SWEPT_FACE",FACE,{"disambiguationData":[OSD([sQuery(id+"F15.wireOp",EDGE,"E10")])]})]});
            fillet(context, id + "F23", {"entities" : qUnion([Q0, Q1, Q2, Q3, Q4, Q5, Q6, Q7, Q8, Q9]), "radius" : 0.2 * mm, "tangentPropagation" : true, "allowEdgeOverflow" : false});
        }
        {
            var Q0;
            {var subQ0=sQuery(id+"F2.wireOp",EDGE,"E1.left");Q0=makeQuery(id+"F7.boolean.opBoolean","SPLIT",EDGE,{"disambiguationData":[TD([makeQuery(id+"F3.boolean.opBoolean","COPY",FACE,{"derivedFrom":makeQuery(id+"F3.opExtrude","SWEPT_FACE",FACE,{"disambiguationData":[OSD([sQuery(id+"F2.wireOp",EDGE,"E1.top")])]})})])],"derivedFrom":makeQuery(id+"F3.boolean.opBoolean","COPY",EDGE,{"derivedFrom":makeQuery(id+"F3.opExtrude","CAP_EDGE",EDGE,{"disambiguationData":[OSD([subQ0])],"isStart":true})})});}
            var Q1;
            Q1=makeQuery(id+"F8.opFillet","BLEND_EDGE",EDGE,{"blendedFrom":[makeQuery(id+"F3.boolean.opBoolean","COPY",EDGE,{"derivedFrom":makeQuery(id+"F3.opExtrude","SWEPT_EDGE",EDGE,{"disambiguationData":[OSD([sQuery(id+"F2.wireOp",EDGE,"E1.top"),sQuery(id+"F2.wireOp",EDGE,"E1.left")])]})}),makeQuery(id+"F1.opExtrude","CAP_FACE",FACE,{"disambiguationData":[OSD([sQuery(id+"F0.wireOp",EDGE,"E0.bottom"),sQuery(id+"F0.wireOp",EDGE,"E0.top"),sQuery(id+"F0.wireOp",EDGE,"E0.left"),sQuery(id+"F0.wireOp",EDGE,"E0.right")])],"isStart":false})],"blendedInto":[makeQuery(id+"F1.opExtrude","CAP_FACE",FACE,{"disambiguationData":[OSD([sQuery(id+"F0.wireOp",EDGE,"E0.bottom"),sQuery(id+"F0.wireOp",EDGE,"E0.top"),sQuery(id+"F0.wireOp",EDGE,"E0.left"),sQuery(id+"F0.wireOp",EDGE,"E0.right")])],"isStart":false})]});
            var Q2;
            {var subQ0=sQuery(id+"F2.wireOp",EDGE,"E1.left");Q2=makeQuery(id+"F7.boolean.opBoolean","SPLIT",EDGE,{"disambiguationData":[TD([makeQuery(id+"F3.boolean.opBoolean","COPY",FACE,{"derivedFrom":makeQuery(id+"F3.opExtrude","SWEPT_FACE",FACE,{"disambiguationData":[OSD([sQuery(id+"F2.wireOp",EDGE,"E1.bottom")])]})})])],"derivedFrom":makeQuery(id+"F3.boolean.opBoolean","COPY",EDGE,{"derivedFrom":makeQuery(id+"F3.opExtrude","CAP_EDGE",EDGE,{"disambiguationData":[OSD([subQ0])],"isStart":true})})});}
            var Q3;
            {var subQ4=sQuery(id+"F2.wireOp",EDGE,"E1.bottom");var subQ5=sQuery(id+"F2.wireOp",EDGE,"E1.left");Q3=makeQuery(id+"F8.opFillet","BLEND_EDGE",EDGE,{"blendedFrom":[makeQuery(id+"F3.boolean.opBoolean","COPY",EDGE,{"derivedFrom":makeQuery(id+"F3.opExtrude","SWEPT_EDGE",EDGE,{"disambiguationData":[OSD([subQ4,subQ5])]})}),makeQuery(id+"F7.boolean.opBoolean","SPLIT",FACE,{"disambiguationData":[TD([makeQuery(id+"F3.boolean.opBoolean","COPY",FACE,{"derivedFrom":makeQuery(id+"F3.opExtrude","SWEPT_FACE",FACE,{"disambiguationData":[OSD([subQ4])]})})])],"derivedFrom":makeQuery(id+"F3.boolean.opBoolean","COPY",FACE,{"derivedFrom":makeQuery(id+"F3.opExtrude","SWEPT_FACE",FACE,{"disambiguationData":[OSD([subQ5])]})})})],"blendedInto":[makeQuery(id+"F7.boolean.opBoolean","SPLIT",FACE,{"disambiguationData":[TD([makeQuery(id+"F3.boolean.opBoolean","COPY",FACE,{"derivedFrom":makeQuery(id+"F3.opExtrude","SWEPT_FACE",FACE,{"disambiguationData":[OSD([subQ4])]})})])],"derivedFrom":makeQuery(id+"F3.boolean.opBoolean","COPY",FACE,{"derivedFrom":makeQuery(id+"F3.opExtrude","SWEPT_FACE",FACE,{"disambiguationData":[OSD([subQ5])]})})})]});}
            var Q4;
            Q4=makeQuery(id+"F8.opFillet","BLEND_EDGE",EDGE,{"blendedFrom":[makeQuery(id+"F3.boolean.opBoolean","COPY",EDGE,{"derivedFrom":makeQuery(id+"F3.opExtrude","SWEPT_EDGE",EDGE,{"disambiguationData":[OSD([sQuery(id+"F2.wireOp",EDGE,"E1.bottom"),sQuery(id+"F2.wireOp",EDGE,"E1.left")])]})}),makeQuery(id+"F1.opExtrude","CAP_FACE",FACE,{"disambiguationData":[OSD([sQuery(id+"F0.wireOp",EDGE,"E0.bottom"),sQuery(id+"F0.wireOp",EDGE,"E0.top"),sQuery(id+"F0.wireOp",EDGE,"E0.left"),sQuery(id+"F0.wireOp",EDGE,"E0.right")])],"isStart":false})],"blendedInto":[makeQuery(id+"F1.opExtrude","CAP_FACE",FACE,{"disambiguationData":[OSD([sQuery(id+"F0.wireOp",EDGE,"E0.bottom"),sQuery(id+"F0.wireOp",EDGE,"E0.top"),sQuery(id+"F0.wireOp",EDGE,"E0.left"),sQuery(id+"F0.wireOp",EDGE,"E0.right")])],"isStart":false})]});
            var Q5;
            {var subQ0=makeQuery(id+"F1.opExtrude","CAP_FACE",FACE,{"disambiguationData":[OSD([sQuery(id+"F0.wireOp",EDGE,"E0.bottom"),sQuery(id+"F0.wireOp",EDGE,"E0.top"),sQuery(id+"F0.wireOp",EDGE,"E0.left"),sQuery(id+"F0.wireOp",EDGE,"E0.right")])],"isStart":true});var subQ1=makeQuery(id+"F3.opExtrude","SWEPT_FACE",FACE,{"disambiguationData":[OSD([sQuery(id+"F2.wireOp",EDGE,"E1.left")])]});Q5=makeQuery(id+"F7.boolean.opBoolean","SPLIT",EDGE,{"disambiguationData":[TD([makeQuery(id+"F3.boolean.opBoolean","COPY",FACE,{"derivedFrom":makeQuery(id+"F3.opExtrude","SWEPT_FACE",FACE,{"disambiguationData":[OSD([sQuery(id+"F2.wireOp",EDGE,"E1.bottom")])]})})])],"derivedFrom":makeQuery(id+"F3.boolean.opBoolean","INTERSECT",EDGE,{"derivedFrom":[subQ0,subQ1]})});}
            var Q6;
            {var subQ0=makeQuery(id+"F1.opExtrude","CAP_FACE",FACE,{"disambiguationData":[OSD([sQuery(id+"F0.wireOp",EDGE,"E0.bottom"),sQuery(id+"F0.wireOp",EDGE,"E0.top"),sQuery(id+"F0.wireOp",EDGE,"E0.left"),sQuery(id+"F0.wireOp",EDGE,"E0.right")])],"isStart":true});var subQ1=makeQuery(id+"F3.opExtrude","SWEPT_FACE",FACE,{"disambiguationData":[OSD([sQuery(id+"F2.wireOp",EDGE,"E1.left")])]});Q6=makeQuery(id+"F7.boolean.opBoolean","SPLIT",EDGE,{"disambiguationData":[TD([makeQuery(id+"F3.boolean.opBoolean","COPY",FACE,{"derivedFrom":makeQuery(id+"F3.opExtrude","SWEPT_FACE",FACE,{"disambiguationData":[OSD([sQuery(id+"F2.wireOp",EDGE,"E1.top")])]})})])],"derivedFrom":makeQuery(id+"F3.boolean.opBoolean","INTERSECT",EDGE,{"derivedFrom":[subQ0,subQ1]})});}
            var Q7;
            Q7=makeQuery(id+"F8.opFillet","BLEND_EDGE",EDGE,{"blendedFrom":[makeQuery(id+"F3.boolean.opBoolean","COPY",EDGE,{"derivedFrom":makeQuery(id+"F3.opExtrude","SWEPT_EDGE",EDGE,{"disambiguationData":[OSD([sQuery(id+"F2.wireOp",EDGE,"E1.bottom"),sQuery(id+"F2.wireOp",EDGE,"E1.left")])]})}),makeQuery(id+"F1.opExtrude","CAP_FACE",FACE,{"disambiguationData":[OSD([sQuery(id+"F0.wireOp",EDGE,"E0.bottom"),sQuery(id+"F0.wireOp",EDGE,"E0.top"),sQuery(id+"F0.wireOp",EDGE,"E0.left"),sQuery(id+"F0.wireOp",EDGE,"E0.right")])],"isStart":true})],"blendedInto":[makeQuery(id+"F1.opExtrude","CAP_FACE",FACE,{"disambiguationData":[OSD([sQuery(id+"F0.wireOp",EDGE,"E0.bottom"),sQuery(id+"F0.wireOp",EDGE,"E0.top"),sQuery(id+"F0.wireOp",EDGE,"E0.left"),sQuery(id+"F0.wireOp",EDGE,"E0.right")])],"isStart":true})]});
            var Q8;
            Q8=makeQuery(id+"F8.opFillet","BLEND_EDGE",EDGE,{"blendedFrom":[makeQuery(id+"F3.boolean.opBoolean","COPY",EDGE,{"derivedFrom":makeQuery(id+"F3.opExtrude","SWEPT_EDGE",EDGE,{"disambiguationData":[OSD([sQuery(id+"F2.wireOp",EDGE,"E1.top"),sQuery(id+"F2.wireOp",EDGE,"E1.left")])]})}),makeQuery(id+"F1.opExtrude","CAP_FACE",FACE,{"disambiguationData":[OSD([sQuery(id+"F0.wireOp",EDGE,"E0.bottom"),sQuery(id+"F0.wireOp",EDGE,"E0.top"),sQuery(id+"F0.wireOp",EDGE,"E0.left"),sQuery(id+"F0.wireOp",EDGE,"E0.right")])],"isStart":true})],"blendedInto":[makeQuery(id+"F1.opExtrude","CAP_FACE",FACE,{"disambiguationData":[OSD([sQuery(id+"F0.wireOp",EDGE,"E0.bottom"),sQuery(id+"F0.wireOp",EDGE,"E0.top"),sQuery(id+"F0.wireOp",EDGE,"E0.left"),sQuery(id+"F0.wireOp",EDGE,"E0.right")])],"isStart":true})]});
            fillet(context, id + "F24", {"entities" : qUnion([Q0, Q1, Q2, Q3, Q4, Q5, Q6, Q7, Q8]), "radius" : 1.5 * mm, "allowEdgeOverflow" : false});
        }
        {
            var Q0;
            Q0=makeQuery(id+"F3.boolean.opBoolean","INTERSECT",EDGE,{"derivedFrom":[makeQuery(id+"F1.opExtrude","CAP_FACE",FACE,{"disambiguationData":[OSD([sQuery(id+"F0.wireOp",EDGE,"E0.bottom"),sQuery(id+"F0.wireOp",EDGE,"E0.top"),sQuery(id+"F0.wireOp",EDGE,"E0.left"),sQuery(id+"F0.wireOp",EDGE,"E0.right")])],"isStart":true}),makeQuery(id+"F3.opExtrude","SWEPT_FACE",FACE,{"disambiguationData":[OSD([sQuery(id+"F2.wireOp",EDGE,"E1.bottom")])]})]});
            var Q1;
            Q1=makeQuery(id+"F8.opFillet","BLEND_EDGE",EDGE,{"blendedFrom":[makeQuery(id+"F3.boolean.opBoolean","COPY",EDGE,{"derivedFrom":makeQuery(id+"F3.opExtrude","SWEPT_EDGE",EDGE,{"disambiguationData":[OSD([sQuery(id+"F2.wireOp",EDGE,"E1.bottom"),sQuery(id+"F2.wireOp",EDGE,"E1.right")])]})}),makeQuery(id+"F1.opExtrude","CAP_FACE",FACE,{"disambiguationData":[OSD([sQuery(id+"F0.wireOp",EDGE,"E0.bottom"),sQuery(id+"F0.wireOp",EDGE,"E0.top"),sQuery(id+"F0.wireOp",EDGE,"E0.left"),sQuery(id+"F0.wireOp",EDGE,"E0.right")])],"isStart":false})],"blendedInto":[makeQuery(id+"F1.opExtrude","CAP_FACE",FACE,{"disambiguationData":[OSD([sQuery(id+"F0.wireOp",EDGE,"E0.bottom"),sQuery(id+"F0.wireOp",EDGE,"E0.top"),sQuery(id+"F0.wireOp",EDGE,"E0.left"),sQuery(id+"F0.wireOp",EDGE,"E0.right")])],"isStart":false})]});
            fillet(context, id + "F25", {"entities" : qUnion([Q0, Q1]), "radius" : 0.5 * mm, "tangentPropagation" : true, "allowEdgeOverflow" : false});
        }
        {
            var Q0;
            {var subQ0=sQuery(id+"F0.wireOp",EDGE,"E0.bottom");var subQ1=sQuery(id+"F0.wireOp",EDGE,"E0.left");Q0=makeQuery(id+"F7.boolean.opBoolean","SPLIT",EDGE,{"disambiguationData":[TD([makeQuery(id+"F1.opExtrude","SWEPT_FACE",FACE,{"disambiguationData":[OSD([subQ0])]})])],"derivedFrom":makeQuery(id+"F1.opExtrude","CAP_EDGE",EDGE,{"disambiguationData":[OSD([subQ1])],"isStart":false})});}
            var Q1;
            {var subQ0=sQuery(id+"F0.wireOp",EDGE,"E0.left");var subQ1=sQuery(id+"F0.wireOp",EDGE,"E0.top");Q1=makeQuery(id+"F7.boolean.opBoolean","SPLIT",EDGE,{"disambiguationData":[TD([makeQuery(id+"F1.opExtrude","SWEPT_FACE",FACE,{"disambiguationData":[OSD([subQ1])]})])],"derivedFrom":makeQuery(id+"F1.opExtrude","CAP_EDGE",EDGE,{"disambiguationData":[OSD([subQ0])],"isStart":false})});}
            var Q2;
            {var subQ0=sQuery(id+"F0.wireOp",EDGE,"E0.bottom");var subQ1=sQuery(id+"F0.wireOp",EDGE,"E0.left");Q2=makeQuery(id+"F7.boolean.opBoolean","SPLIT",EDGE,{"disambiguationData":[TD([makeQuery(id+"F1.opExtrude","SWEPT_FACE",FACE,{"disambiguationData":[OSD([subQ0])]})])],"derivedFrom":makeQuery(id+"F1.opExtrude","CAP_EDGE",EDGE,{"disambiguationData":[OSD([subQ1])],"isStart":true})});}
            var Q3;
            {var subQ0=sQuery(id+"F0.wireOp",EDGE,"E0.left");var subQ1=sQuery(id+"F0.wireOp",EDGE,"E0.top");Q3=makeQuery(id+"F7.boolean.opBoolean","SPLIT",EDGE,{"disambiguationData":[TD([makeQuery(id+"F1.opExtrude","SWEPT_FACE",FACE,{"disambiguationData":[OSD([subQ1])]})])],"derivedFrom":makeQuery(id+"F1.opExtrude","CAP_EDGE",EDGE,{"disambiguationData":[OSD([subQ0])],"isStart":true})});}
            fillet(context, id + "F26", {"entities" : qUnion([Q0, Q1, Q2, Q3]), "radius" : 0.2 * mm, "tangentPropagation" : true, "allowEdgeOverflow" : false});
        }
        {
            var Q0;
            Q0=makeQuery(id+"F14.boolean.opBoolean","COPY",EDGE,{"derivedFrom":makeQuery(id+"F14.opExtrude","CAP_EDGE",EDGE,{"disambiguationData":[OSD([sQuery(id+"F13.wireOp",EDGE,"E9")])],"isStart":false})});
            fillet(context, id + "F27", {"entities" : qUnion([Q0]), "radius" : 0.2 * mm, "tangentPropagation" : true, "allowEdgeOverflow" : false});
        }
        {
            var Q0;
            Q0=makeQuery(id+"F14.boolean.opBoolean","INTERSECT",EDGE,{"derivedFrom":[makeQuery(id+"F1.opExtrude","CAP_FACE",FACE,{"disambiguationData":[OSD([sQuery(id+"F0.wireOp",EDGE,"E0.bottom"),sQuery(id+"F0.wireOp",EDGE,"E0.top"),sQuery(id+"F0.wireOp",EDGE,"E0.left"),sQuery(id+"F0.wireOp",EDGE,"E0.right")])],"isStart":false}),makeQuery(id+"F14.opExtrude","CAP_FACE",FACE,{"disambiguationData":[OSD([sQuery(id+"F13.wireOp",EDGE,"E9")])],"isStart":false})]});
            fillet(context, id + "F28", {"entities" : qUnion([Q0]), "radius" : 0.2 * mm, "tangentPropagation" : true, "allowEdgeOverflow" : false});
        }
    });
